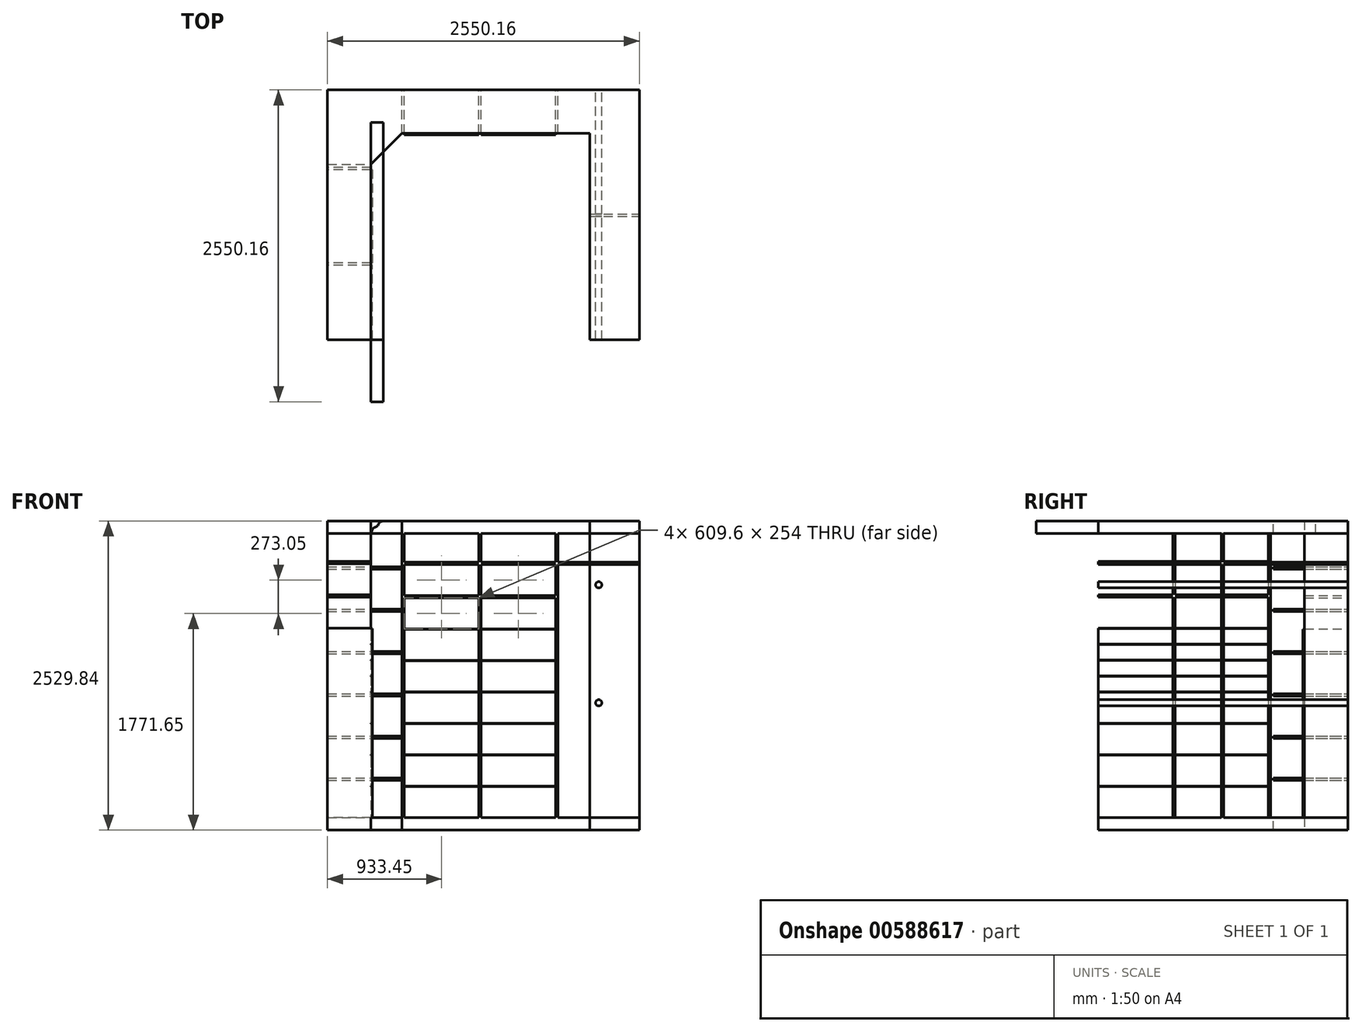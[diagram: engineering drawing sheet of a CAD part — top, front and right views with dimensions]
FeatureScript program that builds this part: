
annotation { "Feature Type Name" : "Feature", "Feature Type Description" : "" }
export const myFeature = defineFeature(function(context is Context, id is Id, definition is map)
    precondition{}
    {
        {
            var Q0;
            Q0=qCreatedBy(makeId("Top.planeOp"),FACE);
            var sketch = newSketch(context, id + "F0", { "sketchPlane" : qUnion([Q0])});
            skLineSegment(sketch, "E0.bottom", {"start": v(-1275.08, 1021.08) * mm, "end": v(1275.08, 1021.08) * mm});
            skLineSegment(sketch, "E0.top", {"start": v(-1275.08, -1021.08) * mm, "end": v(1275.08, -1021.08) * mm});
            skLineSegment(sketch, "E0.left", {"start": v(-1275.08, 1021.08) * mm, "end": v(-1275.08, -1021.08) * mm});
            skLineSegment(sketch, "E0.right", {"start": v(1275.08, 1021.08) * mm, "end": v(1275.08, -1021.08) * mm});
            skPoint(sketch, "E1", {"position": v(-1275.08, 0) * mm});
            skPoint(sketch, "E2", {"position": v(0, 1021.08) * mm});
            skArc(sketch, "E3", {"start": v(-68.07, -1021.08) * mm, "mid": v(139.94, -518.9) * mm, "end": v(642.11, -310.9) * mm, "construction": true});
            skLineSegment(sketch, "E4", {"start": v(642.11, -310.9) * mm, "end": v(642.11, -1021.08) * mm, "construction": true});
            skLineSegment(sketch, "E5", {"start": v(-919.48, -1021.08) * mm, "end": v(-919.48, 411.48) * mm});
            skLineSegment(sketch, "E6", {"start": v(-919.48, 411.48) * mm, "end": v(-665.48, 665.48) * mm});
            skLineSegment(sketch, "E7", {"start": v(-665.48, 665.48) * mm, "end": v(868.68, 665.48) * mm});
            skLineSegment(sketch, "E8", {"start": v(868.68, 665.48) * mm, "end": v(868.68, -1021.08) * mm});
            skLineSegment(sketch, "E9", {"start": v(-665.48, 1021.08) * mm, "end": v(-665.48, 411.48) * mm});
            skLineSegment(sketch, "E10", {"start": v(-665.48, 411.48) * mm, "end": v(-1275.08, 411.48) * mm});
            skSolve(sketch);
        }
        {
            var Q0;
            Q0=qCreatedBy(makeId("Front.planeOp"),FACE);
            var Q1;
            Q1=sQuery(id+"F0.wireOp",VERTEX,"E0.bottom.start");
            cPlane(context, id + "F1", {"entities" : qUnion([Q0, Q1]), "cplaneType" : CPlaneType.PLANE_POINT, "offset" : 25.4 * mm, "width" : 152.4 * mm, "height" : 152.4 * mm});
        }
        {
            var Q0;
            Q0=qCreatedBy(id+"F1.planeOp",FACE);
            var sketch = newSketch(context, id + "F2", { "sketchPlane" : qUnion([Q0])});
            skLineSegment(sketch, "E11.bottom", {"start": v(-1275.08, 2529.84) * mm, "end": v(1275.08, 2529.84) * mm});
            skLineSegment(sketch, "E11.top", {"start": v(-1275.08, 0) * mm, "end": v(1275.08, 0) * mm});
            skLineSegment(sketch, "E11.left", {"start": v(-1275.08, 2529.84) * mm, "end": v(-1275.08, 0) * mm});
            skLineSegment(sketch, "E11.right", {"start": v(1275.08, 2529.84) * mm, "end": v(1275.08, 0) * mm});
            skLineSegment(sketch, "E12", {"start": v(-1275.08, 101.6) * mm, "end": v(1275.08, 101.6) * mm});
            skLineSegment(sketch, "E13", {"start": v(-36.83, 101.6) * mm, "end": v(-36.83, 2529.84) * mm});
            skLineSegment(sketch, "E14", {"start": v(-17.78, 101.6) * mm, "end": v(-17.78, 2529.84) * mm});
            skLineSegment(sketch, "E15", {"start": v(-665.48, 2529.84) * mm, "end": v(-665.48, 0) * mm});
            skLineSegment(sketch, "E16", {"start": v(-646.43, 2529.84) * mm, "end": v(-646.43, 0) * mm});
            skLineSegment(sketch, "E17", {"start": v(591.82, 2529.84) * mm, "end": v(591.82, 101.6) * mm});
            skLineSegment(sketch, "E18", {"start": v(610.87, 2529.84) * mm, "end": v(610.87, 101.6) * mm});
            skLineSegment(sketch, "E19", {"start": v(-36.83, 245.4) * mm, "end": v(-17.78, 245.4) * mm, "construction": true});
            skLineSegment(sketch, "E20", {"start": v(-665.48, 245.4) * mm, "end": v(-646.43, 245.4) * mm, "construction": true});
            skLineSegment(sketch, "E21", {"start": v(591.82, 245.4) * mm, "end": v(610.87, 245.4) * mm, "construction": true});
            skLineSegment(sketch, "E22", {"start": v(-646.43, 245.4) * mm, "end": v(-36.83, 245.4) * mm, "construction": true});
            skLineSegment(sketch, "E23", {"start": v(-17.78, 245.4) * mm, "end": v(591.82, 245.4) * mm, "construction": true});
            skLineSegment(sketch, "E24", {"start": v(-646.43, 355.6) * mm, "end": v(591.82, 355.6) * mm});
            skLineSegment(sketch, "E25", {"start": v(-646.43, 358.78) * mm, "end": v(591.82, 358.78) * mm});
            skLineSegment(sketch, "E26.0.1.0", {"start": v(-646.43, 612.77) * mm, "end": v(591.82, 612.77) * mm});
            skLineSegment(sketch, "E26.0.1.1", {"start": v(-646.43, 615.95) * mm, "end": v(591.82, 615.95) * mm});
            skLineSegment(sketch, "E26.0.2.0", {"start": v(-646.43, 869.95) * mm, "end": v(591.82, 869.95) * mm});
            skLineSegment(sketch, "E26.0.2.1", {"start": v(-646.43, 873.12) * mm, "end": v(591.82, 873.12) * mm});
            skLineSegment(sketch, "E26.0.3.0", {"start": v(-646.43, 1127.12) * mm, "end": v(591.82, 1127.12) * mm});
            skLineSegment(sketch, "E26.0.3.1", {"start": v(-646.43, 1130.3) * mm, "end": v(591.82, 1130.3) * mm});
            skLineSegment(sketch, "E26.0.4.0", {"start": v(-646.43, 1384.3) * mm, "end": v(591.82, 1384.3) * mm});
            skLineSegment(sketch, "E26.0.4.1", {"start": v(-646.43, 1387.47) * mm, "end": v(591.82, 1387.47) * mm});
            skLineSegment(sketch, "E26.direction1", {"start": v(-646.43, 355.6) * mm, "end": v(-621.03, 355.6) * mm, "construction": true});
            skLineSegment(sketch, "E26.direction2", {"start": v(-646.43, 355.6) * mm, "end": v(-646.43, 612.77) * mm, "construction": true});
            skLineSegment(sketch, "E27.0.0.5", {"start": v(-646.43, 1641.47) * mm, "end": v(591.82, 1641.47) * mm});
            skLineSegment(sketch, "E27.3.0.5", {"start": v(-646.43, 1644.65) * mm, "end": v(591.82, 1644.65) * mm});
            skLineSegment(sketch, "E28", {"start": v(-1275.08, 2428.24) * mm, "end": v(1275.08, 2428.24) * mm});
            skLineSegment(sketch, "E29", {"start": v(-646.43, 1898.65) * mm, "end": v(591.82, 1898.65) * mm});
            skLineSegment(sketch, "E30", {"start": v(-646.43, 1917.7) * mm, "end": v(591.82, 1917.7) * mm});
            skLineSegment(sketch, "E31.0.1.0", {"start": v(-646.43, 2171.7) * mm, "end": v(591.82, 2171.7) * mm});
            skLineSegment(sketch, "E31.0.1.1", {"start": v(-646.43, 2190.75) * mm, "end": v(591.82, 2190.75) * mm});
            skLineSegment(sketch, "E31.direction1", {"start": v(-646.43, 1898.65) * mm, "end": v(-646.43, 1898.65) * mm});
            skLineSegment(sketch, "E31.direction2", {"start": v(-646.43, 1898.65) * mm, "end": v(-646.43, 2171.7) * mm, "construction": true});
            skCircle(sketch, "E32", {"center": v(942.98, 2006.6) * mm, "radius": 25.4 * mm});
            skLineSegment(sketch, "E33", {"start": v(610.87, 245.4) * mm, "end": v(1275.08, 245.4) * mm, "construction": true});
            skPoint(sketch, "E34", {"position": v(942.97, 245.4) * mm});
            skLineSegment(sketch, "E35", {"start": v(942.98, 2428.24) * mm, "end": v(942.98, 101.6) * mm, "construction": true});
            skLineSegment(sketch, "E36", {"start": v(610.87, 2171.7) * mm, "end": v(1275.08, 2171.7) * mm});
            skLineSegment(sketch, "E37", {"start": v(610.87, 2190.75) * mm, "end": v(1275.08, 2190.75) * mm});
            skCircle(sketch, "E38", {"center": v(942.98, 1041.4) * mm, "radius": 25.4 * mm});
            skLineSegment(sketch, "E39", {"start": v(-1275.08, 406.4) * mm, "end": v(-665.48, 406.4) * mm});
            skLineSegment(sketch, "E40", {"start": v(-1275.08, 425.45) * mm, "end": v(-665.48, 425.45) * mm});
            skLineSegment(sketch, "E41.0.1.0", {"start": v(-1275.08, 751.84) * mm, "end": v(-665.48, 751.84) * mm});
            skLineSegment(sketch, "E41.0.1.1", {"start": v(-1275.08, 770.9) * mm, "end": v(-665.48, 770.9) * mm});
            skLineSegment(sketch, "E41.0.2.0", {"start": v(-1275.08, 1097.28) * mm, "end": v(-665.48, 1097.28) * mm});
            skLineSegment(sketch, "E41.0.2.1", {"start": v(-1275.08, 1116.33) * mm, "end": v(-665.48, 1116.33) * mm});
            skLineSegment(sketch, "E41.0.3.0", {"start": v(-1275.08, 1442.72) * mm, "end": v(-665.48, 1442.72) * mm});
            skLineSegment(sketch, "E41.0.3.1", {"start": v(-1275.08, 1461.77) * mm, "end": v(-665.48, 1461.77) * mm});
            skLineSegment(sketch, "E41.0.4.0", {"start": v(-1275.08, 1788.16) * mm, "end": v(-665.48, 1788.16) * mm});
            skLineSegment(sketch, "E41.0.4.1", {"start": v(-1275.08, 1807.2) * mm, "end": v(-665.48, 1807.2) * mm});
            skLineSegment(sketch, "E41.0.5.0", {"start": v(-1275.08, 2133.6) * mm, "end": v(-665.48, 2133.6) * mm});
            skLineSegment(sketch, "E41.0.5.1", {"start": v(-1275.08, 2152.65) * mm, "end": v(-665.48, 2152.65) * mm});
            skLineSegment(sketch, "E41.direction1", {"start": v(-1275.08, 406.4) * mm, "end": v(-1275.08, 406.4) * mm});
            skLineSegment(sketch, "E41.direction2", {"start": v(-1275.08, 406.4) * mm, "end": v(-1275.08, 751.84) * mm, "construction": true});
            skLineSegment(sketch, "E42", {"start": v(-665.48, 245.4) * mm, "end": v(-1275.08, 245.4) * mm, "construction": true});
            skSolve(sketch);
        }
        {
            var Q0;
            Q0=qCreatedBy(makeId("Right.planeOp"),FACE);
            var Q1;
            Q1=sQuery(id+"F0.wireOp",VERTEX,"E0.left.end");
            cPlane(context, id + "F3", {"entities" : qUnion([Q0, Q1]), "cplaneType" : CPlaneType.PLANE_POINT, "offset" : 25.4 * mm, "width" : 152.4 * mm, "height" : 152.4 * mm});
        }
        {
            var Q0;
            Q0=qCreatedBy(id+"F3.planeOp",FACE);
            var sketch = newSketch(context, id + "F4", { "sketchPlane" : qUnion([Q0])});
            skLineSegment(sketch, "E43.bottom", {"start": v(-1021.08, 0) * mm, "end": v(1021.08, 0) * mm});
            skLineSegment(sketch, "E43.top", {"start": v(-1021.08, 2529.84) * mm, "end": v(1021.08, 2529.84) * mm});
            skLineSegment(sketch, "E43.left", {"start": v(-1021.08, 0) * mm, "end": v(-1021.08, 2529.84) * mm});
            skLineSegment(sketch, "E43.right", {"start": v(1021.08, 0) * mm, "end": v(1021.08, 2529.84) * mm});
            skLineSegment(sketch, "E44", {"start": v(1021.08, 2428.24) * mm, "end": v(-1021.08, 2428.24) * mm});
            skLineSegment(sketch, "E45", {"start": v(1021.08, 101.6) * mm, "end": v(-1021.08, 101.6) * mm});
            skLineSegment(sketch, "E46", {"start": v(-411.48, 2428.24) * mm, "end": v(-411.48, 101.6) * mm});
            skLineSegment(sketch, "E47", {"start": v(-392.43, 2428.24) * mm, "end": v(-392.43, 101.6) * mm});
            skLineSegment(sketch, "E48", {"start": v(369.57, 2428.24) * mm, "end": v(369.57, 101.6) * mm});
            skLineSegment(sketch, "E49", {"start": v(388.62, 2428.24) * mm, "end": v(388.62, 101.6) * mm});
            skLineSegment(sketch, "E50", {"start": v(-1021.08, 216.84) * mm, "end": v(-411.48, 216.84) * mm, "construction": true});
            skLineSegment(sketch, "E51", {"start": v(-411.48, 216.84) * mm, "end": v(-392.43, 216.84) * mm, "construction": true});
            skLineSegment(sketch, "E52", {"start": v(-392.43, 216.84) * mm, "end": v(369.57, 216.84) * mm, "construction": true});
            skLineSegment(sketch, "E53", {"start": v(369.57, 216.84) * mm, "end": v(388.62, 216.84) * mm, "construction": true});
            skLineSegment(sketch, "E54", {"start": v(388.62, 216.84) * mm, "end": v(1021.08, 216.84) * mm, "construction": true});
            skLineSegment(sketch, "E55", {"start": v(-1021.08, 1130.3) * mm, "end": v(369.57, 1130.3) * mm});
            skLineSegment(sketch, "E56", {"start": v(-1021.08, 1127.12) * mm, "end": v(369.57, 1127.12) * mm});
            skLineSegment(sketch, "E57", {"start": v(-1021.08, 355.6) * mm, "end": v(369.57, 355.6) * mm});
            skLineSegment(sketch, "E58", {"start": v(-1021.08, 358.77) * mm, "end": v(369.57, 358.77) * mm});
            skLineSegment(sketch, "E59.0.1.0", {"start": v(-1021.08, 1257.3) * mm, "end": v(369.57, 1257.3) * mm});
            skLineSegment(sketch, "E59.0.1.1", {"start": v(-1021.08, 1260.47) * mm, "end": v(369.57, 1260.47) * mm});
            skLineSegment(sketch, "E59.0.2.0", {"start": v(-1021.08, 1387.47) * mm, "end": v(369.57, 1387.47) * mm});
            skLineSegment(sketch, "E59.0.2.1", {"start": v(-1021.08, 1390.65) * mm, "end": v(369.57, 1390.65) * mm});
            skLineSegment(sketch, "E59.0.3.0", {"start": v(-1021.08, 1517.65) * mm, "end": v(369.57, 1517.65) * mm});
            skLineSegment(sketch, "E59.0.3.1", {"start": v(-1021.08, 1520.82) * mm, "end": v(369.57, 1520.82) * mm});
            skLineSegment(sketch, "E59.0.4.0", {"start": v(-1021.08, 1647.82) * mm, "end": v(369.57, 1647.82) * mm});
            skLineSegment(sketch, "E59.0.4.1", {"start": v(-1021.08, 1651) * mm, "end": v(369.57, 1651) * mm});
            skLineSegment(sketch, "E59.direction1", {"start": v(-1021.08, 1127.12) * mm, "end": v(-995.68, 1127.12) * mm, "construction": true});
            skLineSegment(sketch, "E59.direction2", {"start": v(-1021.08, 1127.12) * mm, "end": v(-1021.08, 1257.3) * mm, "construction": true});
            skLineSegment(sketch, "E60.0.1.0", {"start": v(-1021.08, 612.77) * mm, "end": v(369.57, 612.77) * mm});
            skLineSegment(sketch, "E60.0.1.1", {"start": v(-1021.08, 615.95) * mm, "end": v(369.57, 615.95) * mm});
            skLineSegment(sketch, "E60.0.2.0", {"start": v(-1021.08, 869.95) * mm, "end": v(369.57, 869.95) * mm});
            skLineSegment(sketch, "E60.0.2.1", {"start": v(-1021.08, 873.12) * mm, "end": v(369.57, 873.12) * mm});
            skLineSegment(sketch, "E60.direction1", {"start": v(-1021.08, 355.6) * mm, "end": v(-995.68, 355.6) * mm, "construction": true});
            skLineSegment(sketch, "E60.direction2", {"start": v(-1021.08, 355.6) * mm, "end": v(-1021.08, 612.77) * mm, "construction": true});
            skLineSegment(sketch, "E61", {"start": v(-1021.08, 1905) * mm, "end": v(369.57, 1905) * mm});
            skLineSegment(sketch, "E62", {"start": v(-1021.08, 1924.05) * mm, "end": v(369.57, 1924.05) * mm});
            skLineSegment(sketch, "E63", {"start": v(-1021.08, 2178.05) * mm, "end": v(369.57, 2178.05) * mm});
            skLineSegment(sketch, "E64", {"start": v(-1021.08, 2197.1) * mm, "end": v(369.57, 2197.1) * mm});
            skLineSegment(sketch, "E65", {"start": v(-504.08, 2428.24) * mm, "end": v(-504.08, 2197.1) * mm, "construction": true});
            skLineSegment(sketch, "E66", {"start": v(-504.08, 2197.1) * mm, "end": v(-504.08, 2178.05) * mm, "construction": true});
            skLineSegment(sketch, "E67", {"start": v(-504.08, 2178.05) * mm, "end": v(-504.08, 1924.05) * mm, "construction": true});
            skLineSegment(sketch, "E68", {"start": v(-504.08, 1924.05) * mm, "end": v(-504.08, 1905) * mm, "construction": true});
            skLineSegment(sketch, "E69", {"start": v(-504.08, 1905) * mm, "end": v(-504.08, 1651) * mm, "construction": true});
            skSolve(sketch);
        }
        {
            var Q0;
            Q0=qCreatedBy(makeId("Right.planeOp"),FACE);
            var Q1;
            Q1=sQuery(id+"F0.wireOp",VERTEX,"E0.right.end");
            cPlane(context, id + "F5", {"entities" : qUnion([Q0, Q1]), "cplaneType" : CPlaneType.PLANE_POINT, "offset" : 25.4 * mm, "width" : 152.4 * mm, "height" : 152.4 * mm});
        }
        {
            var Q0;
            Q0=qCreatedBy(id+"F5.planeOp",FACE);
            var sketch = newSketch(context, id + "F6", { "sketchPlane" : qUnion([Q0])});
            skLineSegment(sketch, "E70.bottom", {"start": v(-1021.08, 2529.84) * mm, "end": v(1021.08, 2529.84) * mm});
            skLineSegment(sketch, "E70.top", {"start": v(-1021.08, 0) * mm, "end": v(1021.08, 0) * mm});
            skLineSegment(sketch, "E70.left", {"start": v(-1021.08, 2529.84) * mm, "end": v(-1021.08, 0) * mm});
            skLineSegment(sketch, "E70.right", {"start": v(1021.08, 2529.84) * mm, "end": v(1021.08, 0) * mm});
            skLineSegment(sketch, "E71", {"start": v(5.08, 2529.84) * mm, "end": v(5.08, 101.6) * mm});
            skLineSegment(sketch, "E72", {"start": v(-13.97, 2529.84) * mm, "end": v(-13.97, 101.6) * mm});
            skLineSegment(sketch, "E73", {"start": v(1021.08, 101.6) * mm, "end": v(-1021.08, 101.6) * mm});
            skLineSegment(sketch, "E74", {"start": v(1021.08, 2428.24) * mm, "end": v(-1021.08, 2428.24) * mm});
            skLineSegment(sketch, "E75", {"start": v(1021.08, 2190.75) * mm, "end": v(-1021.08, 2190.75) * mm});
            skLineSegment(sketch, "E76", {"start": v(1021.08, 2171.7) * mm, "end": v(-1021.08, 2171.7) * mm});
            skSolve(sketch);
        }
        {
            var Q0;
            {var subQ0=sQuery(id+"F2.wireOp",EDGE,"E26.0.4.1");var subQ1=sQuery(id+"F2.wireOp",EDGE,"E13");var subQ2=makeQuery(id+"F2.imprint","INTERSECT",VERTEX,{"derivedFrom":[subQ1,subQ0]});Q0=makeQuery(id+"F2.imprint","IMPRINT",FACE,{"disambiguationData":[TD([[makeQuery(id+"F2.imprint","IMPRINT",EDGE,{"disambiguationData":[TD([[subQ2,-1.0]])],"derivedFrom":subQ1}),-1.0]])]});}
            var Q1;
            {var subQ0=sQuery(id+"F2.wireOp",EDGE,"E26.0.4.0");var subQ1=sQuery(id+"F2.wireOp",EDGE,"E13");var subQ2=makeQuery(id+"F2.imprint","INTERSECT",VERTEX,{"derivedFrom":[subQ1,subQ0]});Q1=makeQuery(id+"F2.imprint","IMPRINT",FACE,{"disambiguationData":[TD([[makeQuery(id+"F2.imprint","IMPRINT",EDGE,{"disambiguationData":[TD([[subQ2,-1.0]])],"derivedFrom":subQ1}),-1.0]])]});}
            var Q2;
            {var subQ0=sQuery(id+"F2.wireOp",EDGE,"E26.0.3.1");var subQ1=sQuery(id+"F2.wireOp",EDGE,"E13");var subQ2=makeQuery(id+"F2.imprint","INTERSECT",VERTEX,{"derivedFrom":[subQ1,subQ0]});Q2=makeQuery(id+"F2.imprint","IMPRINT",FACE,{"disambiguationData":[TD([[makeQuery(id+"F2.imprint","IMPRINT",EDGE,{"disambiguationData":[TD([[subQ2,-1.0]])],"derivedFrom":subQ1}),-1.0]])]});}
            var Q3;
            {var subQ0=sQuery(id+"F2.wireOp",EDGE,"E26.0.3.0");var subQ1=sQuery(id+"F2.wireOp",EDGE,"E13");var subQ2=makeQuery(id+"F2.imprint","INTERSECT",VERTEX,{"derivedFrom":[subQ1,subQ0]});Q3=makeQuery(id+"F2.imprint","IMPRINT",FACE,{"disambiguationData":[TD([[makeQuery(id+"F2.imprint","IMPRINT",EDGE,{"disambiguationData":[TD([[subQ2,-1.0]])],"derivedFrom":subQ1}),-1.0]])]});}
            var Q4;
            {var subQ0=sQuery(id+"F2.wireOp",EDGE,"E26.0.2.1");var subQ1=sQuery(id+"F2.wireOp",EDGE,"E13");var subQ2=makeQuery(id+"F2.imprint","INTERSECT",VERTEX,{"derivedFrom":[subQ1,subQ0]});Q4=makeQuery(id+"F2.imprint","IMPRINT",FACE,{"disambiguationData":[TD([[makeQuery(id+"F2.imprint","IMPRINT",EDGE,{"disambiguationData":[TD([[subQ2,-1.0]])],"derivedFrom":subQ1}),-1.0]])]});}
            var Q5;
            {var subQ0=sQuery(id+"F2.wireOp",EDGE,"E26.0.2.0");var subQ1=sQuery(id+"F2.wireOp",EDGE,"E13");var subQ2=makeQuery(id+"F2.imprint","INTERSECT",VERTEX,{"derivedFrom":[subQ1,subQ0]});Q5=makeQuery(id+"F2.imprint","IMPRINT",FACE,{"disambiguationData":[TD([[makeQuery(id+"F2.imprint","IMPRINT",EDGE,{"disambiguationData":[TD([[subQ2,-1.0]])],"derivedFrom":subQ1}),-1.0]])]});}
            var Q6;
            {var subQ0=sQuery(id+"F2.wireOp",EDGE,"E26.0.1.1");var subQ1=sQuery(id+"F2.wireOp",EDGE,"E13");var subQ2=makeQuery(id+"F2.imprint","INTERSECT",VERTEX,{"derivedFrom":[subQ1,subQ0]});Q6=makeQuery(id+"F2.imprint","IMPRINT",FACE,{"disambiguationData":[TD([[makeQuery(id+"F2.imprint","IMPRINT",EDGE,{"disambiguationData":[TD([[subQ2,-1.0]])],"derivedFrom":subQ1}),-1.0]])]});}
            var Q7;
            {var subQ0=sQuery(id+"F2.wireOp",EDGE,"E26.0.1.0");var subQ1=sQuery(id+"F2.wireOp",EDGE,"E13");var subQ2=makeQuery(id+"F2.imprint","INTERSECT",VERTEX,{"derivedFrom":[subQ1,subQ0]});Q7=makeQuery(id+"F2.imprint","IMPRINT",FACE,{"disambiguationData":[TD([[makeQuery(id+"F2.imprint","IMPRINT",EDGE,{"disambiguationData":[TD([[subQ2,-1.0]])],"derivedFrom":subQ1}),-1.0]])]});}
            var Q8;
            {var subQ0=sQuery(id+"F2.wireOp",EDGE,"E25");var subQ1=sQuery(id+"F2.wireOp",EDGE,"E13");var subQ2=makeQuery(id+"F2.imprint","INTERSECT",VERTEX,{"derivedFrom":[subQ1,subQ0]});Q8=makeQuery(id+"F2.imprint","IMPRINT",FACE,{"disambiguationData":[TD([[makeQuery(id+"F2.imprint","IMPRINT",EDGE,{"disambiguationData":[TD([[subQ2,-1.0]])],"derivedFrom":subQ1}),-1.0]])]});}
            var Q9;
            {var subQ0=sQuery(id+"F2.wireOp",EDGE,"E24");var subQ1=sQuery(id+"F2.wireOp",EDGE,"E13");var subQ2=makeQuery(id+"F2.imprint","INTERSECT",VERTEX,{"derivedFrom":[subQ1,subQ0]});Q9=makeQuery(id+"F2.imprint","IMPRINT",FACE,{"disambiguationData":[TD([[makeQuery(id+"F2.imprint","IMPRINT",EDGE,{"disambiguationData":[TD([[subQ2,-1.0]])],"derivedFrom":subQ1}),-1.0]])]});}
            var Q10;
            {var subQ0=sQuery(id+"F2.wireOp",EDGE,"E13");var subQ1=sQuery(id+"F2.wireOp",EDGE,"E12");var subQ2=makeQuery(id+"F2.imprint","INTERSECT",VERTEX,{"derivedFrom":[subQ1,subQ0]});Q10=makeQuery(id+"F2.imprint","IMPRINT",FACE,{"disambiguationData":[TD([[makeQuery(id+"F2.imprint","IMPRINT",EDGE,{"disambiguationData":[TD([[subQ2,-1.0]])],"derivedFrom":subQ1}),1.0]])]});}
            extrude(context, id + "F7", {"entities" : qUnion([Q0, Q1, Q2, Q3, Q4, Q5, Q6, Q7, Q8, Q9, Q10]), "depth" : 25.4 * mm, "offsetDistance" : 25.4 * mm});
        }
        {
            var Q0;
            {var subQ11=sQuery(id+"F2.wireOp",EDGE,"E15");var subQ12=sQuery(id+"F2.wireOp",EDGE,"E12");var subQ13=makeQuery(id+"F2.imprint","INTERSECT",VERTEX,{"derivedFrom":[subQ12,subQ11]});Q0=makeQuery(id+"F2.imprint","IMPRINT",FACE,{"disambiguationData":[TD([[makeQuery(id+"F2.imprint","IMPRINT",EDGE,{"disambiguationData":[TD([[subQ13,-1.0]])],"derivedFrom":subQ12}),1.0]])]});}
            var Q1;
            {var subQ0=sQuery(id+"F2.wireOp",EDGE,"E24");var subQ1=sQuery(id+"F2.wireOp",EDGE,"E13");var subQ2=makeQuery(id+"F2.imprint","INTERSECT",VERTEX,{"derivedFrom":[subQ1,subQ0]});Q1=makeQuery(id+"F2.imprint","IMPRINT",FACE,{"disambiguationData":[TD([[makeQuery(id+"F2.imprint","IMPRINT",EDGE,{"disambiguationData":[TD([[subQ2,-1.0]])],"derivedFrom":subQ1}),1.0]])]});}
            var Q2;
            {var subQ0=sQuery(id+"F2.wireOp",EDGE,"E24");var subQ1=sQuery(id+"F2.wireOp",EDGE,"E13");var subQ2=makeQuery(id+"F2.imprint","INTERSECT",VERTEX,{"derivedFrom":[subQ1,subQ0]});Q2=makeQuery(id+"F2.imprint","IMPRINT",FACE,{"disambiguationData":[TD([[makeQuery(id+"F2.imprint","IMPRINT",EDGE,{"disambiguationData":[TD([[subQ2,-1.0]])],"derivedFrom":subQ1}),-1.0]])]});}
            var Q3;
            {var subQ0=sQuery(id+"F2.wireOp",EDGE,"E24");var subQ1=sQuery(id+"F2.wireOp",EDGE,"E14");var subQ2=makeQuery(id+"F2.imprint","INTERSECT",VERTEX,{"derivedFrom":[subQ1,subQ0]});Q3=makeQuery(id+"F2.imprint","IMPRINT",FACE,{"disambiguationData":[TD([[makeQuery(id+"F2.imprint","IMPRINT",EDGE,{"disambiguationData":[TD([[subQ2,-1.0]])],"derivedFrom":subQ1}),-1.0]])]});}
            var Q4;
            {var subQ0=sQuery(id+"F2.wireOp",EDGE,"E26.0.1.0");var subQ1=sQuery(id+"F2.wireOp",EDGE,"E13");var subQ2=makeQuery(id+"F2.imprint","INTERSECT",VERTEX,{"derivedFrom":[subQ1,subQ0]});Q4=makeQuery(id+"F2.imprint","IMPRINT",FACE,{"disambiguationData":[TD([[makeQuery(id+"F2.imprint","IMPRINT",EDGE,{"disambiguationData":[TD([[subQ2,-1.0]])],"derivedFrom":subQ1}),1.0]])]});}
            var Q5;
            {var subQ0=sQuery(id+"F2.wireOp",EDGE,"E26.0.1.0");var subQ1=sQuery(id+"F2.wireOp",EDGE,"E13");var subQ2=makeQuery(id+"F2.imprint","INTERSECT",VERTEX,{"derivedFrom":[subQ1,subQ0]});Q5=makeQuery(id+"F2.imprint","IMPRINT",FACE,{"disambiguationData":[TD([[makeQuery(id+"F2.imprint","IMPRINT",EDGE,{"disambiguationData":[TD([[subQ2,-1.0]])],"derivedFrom":subQ1}),-1.0]])]});}
            var Q6;
            {var subQ0=sQuery(id+"F2.wireOp",EDGE,"E26.0.1.0");var subQ1=sQuery(id+"F2.wireOp",EDGE,"E14");var subQ2=makeQuery(id+"F2.imprint","INTERSECT",VERTEX,{"derivedFrom":[subQ1,subQ0]});Q6=makeQuery(id+"F2.imprint","IMPRINT",FACE,{"disambiguationData":[TD([[makeQuery(id+"F2.imprint","IMPRINT",EDGE,{"disambiguationData":[TD([[subQ2,-1.0]])],"derivedFrom":subQ1}),-1.0]])]});}
            var Q7;
            {var subQ0=sQuery(id+"F2.wireOp",EDGE,"E25");var subQ1=sQuery(id+"F2.wireOp",EDGE,"E13");var subQ2=makeQuery(id+"F2.imprint","INTERSECT",VERTEX,{"derivedFrom":[subQ1,subQ0]});Q7=makeQuery(id+"F2.imprint","IMPRINT",FACE,{"disambiguationData":[TD([[makeQuery(id+"F2.imprint","IMPRINT",EDGE,{"disambiguationData":[TD([[subQ2,-1.0]])],"derivedFrom":subQ1}),-1.0]])]});}
            var Q8;
            {var subQ0=sQuery(id+"F2.wireOp",EDGE,"E13");var subQ1=sQuery(id+"F2.wireOp",EDGE,"E12");var subQ2=makeQuery(id+"F2.imprint","INTERSECT",VERTEX,{"derivedFrom":[subQ1,subQ0]});Q8=makeQuery(id+"F2.imprint","IMPRINT",FACE,{"disambiguationData":[TD([[makeQuery(id+"F2.imprint","IMPRINT",EDGE,{"disambiguationData":[TD([[subQ2,-1.0]])],"derivedFrom":subQ1}),1.0]])]});}
            var Q9;
            {var subQ0=sQuery(id+"F2.wireOp",EDGE,"E26.0.2.0");var subQ1=sQuery(id+"F2.wireOp",EDGE,"E13");var subQ2=makeQuery(id+"F2.imprint","INTERSECT",VERTEX,{"derivedFrom":[subQ1,subQ0]});Q9=makeQuery(id+"F2.imprint","IMPRINT",FACE,{"disambiguationData":[TD([[makeQuery(id+"F2.imprint","IMPRINT",EDGE,{"disambiguationData":[TD([[subQ2,-1.0]])],"derivedFrom":subQ1}),1.0]])]});}
            var Q10;
            {var subQ0=sQuery(id+"F2.wireOp",EDGE,"E26.0.2.0");var subQ1=sQuery(id+"F2.wireOp",EDGE,"E13");var subQ2=makeQuery(id+"F2.imprint","INTERSECT",VERTEX,{"derivedFrom":[subQ1,subQ0]});Q10=makeQuery(id+"F2.imprint","IMPRINT",FACE,{"disambiguationData":[TD([[makeQuery(id+"F2.imprint","IMPRINT",EDGE,{"disambiguationData":[TD([[subQ2,-1.0]])],"derivedFrom":subQ1}),-1.0]])]});}
            var Q11;
            {var subQ0=sQuery(id+"F2.wireOp",EDGE,"E26.0.2.0");var subQ1=sQuery(id+"F2.wireOp",EDGE,"E14");var subQ2=makeQuery(id+"F2.imprint","INTERSECT",VERTEX,{"derivedFrom":[subQ1,subQ0]});Q11=makeQuery(id+"F2.imprint","IMPRINT",FACE,{"disambiguationData":[TD([[makeQuery(id+"F2.imprint","IMPRINT",EDGE,{"disambiguationData":[TD([[subQ2,-1.0]])],"derivedFrom":subQ1}),-1.0]])]});}
            var Q12;
            {var subQ0=sQuery(id+"F2.wireOp",EDGE,"E26.0.1.1");var subQ1=sQuery(id+"F2.wireOp",EDGE,"E13");var subQ2=makeQuery(id+"F2.imprint","INTERSECT",VERTEX,{"derivedFrom":[subQ1,subQ0]});Q12=makeQuery(id+"F2.imprint","IMPRINT",FACE,{"disambiguationData":[TD([[makeQuery(id+"F2.imprint","IMPRINT",EDGE,{"disambiguationData":[TD([[subQ2,-1.0]])],"derivedFrom":subQ1}),-1.0]])]});}
            var Q13;
            {var subQ0=sQuery(id+"F2.wireOp",EDGE,"E26.0.2.1");var subQ1=sQuery(id+"F2.wireOp",EDGE,"E13");var subQ2=makeQuery(id+"F2.imprint","INTERSECT",VERTEX,{"derivedFrom":[subQ1,subQ0]});Q13=makeQuery(id+"F2.imprint","IMPRINT",FACE,{"disambiguationData":[TD([[makeQuery(id+"F2.imprint","IMPRINT",EDGE,{"disambiguationData":[TD([[subQ2,-1.0]])],"derivedFrom":subQ1}),-1.0]])]});}
            var Q14;
            {var subQ0=sQuery(id+"F2.wireOp",EDGE,"E26.0.3.0");var subQ1=sQuery(id+"F2.wireOp",EDGE,"E13");var subQ2=makeQuery(id+"F2.imprint","INTERSECT",VERTEX,{"derivedFrom":[subQ1,subQ0]});Q14=makeQuery(id+"F2.imprint","IMPRINT",FACE,{"disambiguationData":[TD([[makeQuery(id+"F2.imprint","IMPRINT",EDGE,{"disambiguationData":[TD([[subQ2,-1.0]])],"derivedFrom":subQ1}),1.0]])]});}
            var Q15;
            {var subQ0=sQuery(id+"F2.wireOp",EDGE,"E26.0.3.0");var subQ1=sQuery(id+"F2.wireOp",EDGE,"E13");var subQ2=makeQuery(id+"F2.imprint","INTERSECT",VERTEX,{"derivedFrom":[subQ1,subQ0]});Q15=makeQuery(id+"F2.imprint","IMPRINT",FACE,{"disambiguationData":[TD([[makeQuery(id+"F2.imprint","IMPRINT",EDGE,{"disambiguationData":[TD([[subQ2,-1.0]])],"derivedFrom":subQ1}),-1.0]])]});}
            var Q16;
            {var subQ0=sQuery(id+"F2.wireOp",EDGE,"E26.0.3.0");var subQ1=sQuery(id+"F2.wireOp",EDGE,"E14");var subQ2=makeQuery(id+"F2.imprint","INTERSECT",VERTEX,{"derivedFrom":[subQ1,subQ0]});Q16=makeQuery(id+"F2.imprint","IMPRINT",FACE,{"disambiguationData":[TD([[makeQuery(id+"F2.imprint","IMPRINT",EDGE,{"disambiguationData":[TD([[subQ2,-1.0]])],"derivedFrom":subQ1}),-1.0]])]});}
            var Q17;
            {var subQ0=sQuery(id+"F2.wireOp",EDGE,"E26.0.3.1");var subQ1=sQuery(id+"F2.wireOp",EDGE,"E13");var subQ2=makeQuery(id+"F2.imprint","INTERSECT",VERTEX,{"derivedFrom":[subQ1,subQ0]});Q17=makeQuery(id+"F2.imprint","IMPRINT",FACE,{"disambiguationData":[TD([[makeQuery(id+"F2.imprint","IMPRINT",EDGE,{"disambiguationData":[TD([[subQ2,-1.0]])],"derivedFrom":subQ1}),-1.0]])]});}
            var Q18;
            {var subQ0=sQuery(id+"F2.wireOp",EDGE,"E26.0.4.0");var subQ1=sQuery(id+"F2.wireOp",EDGE,"E13");var subQ2=makeQuery(id+"F2.imprint","INTERSECT",VERTEX,{"derivedFrom":[subQ1,subQ0]});Q18=makeQuery(id+"F2.imprint","IMPRINT",FACE,{"disambiguationData":[TD([[makeQuery(id+"F2.imprint","IMPRINT",EDGE,{"disambiguationData":[TD([[subQ2,-1.0]])],"derivedFrom":subQ1}),1.0]])]});}
            var Q19;
            {var subQ0=sQuery(id+"F2.wireOp",EDGE,"E26.0.4.0");var subQ1=sQuery(id+"F2.wireOp",EDGE,"E13");var subQ2=makeQuery(id+"F2.imprint","INTERSECT",VERTEX,{"derivedFrom":[subQ1,subQ0]});Q19=makeQuery(id+"F2.imprint","IMPRINT",FACE,{"disambiguationData":[TD([[makeQuery(id+"F2.imprint","IMPRINT",EDGE,{"disambiguationData":[TD([[subQ2,-1.0]])],"derivedFrom":subQ1}),-1.0]])]});}
            var Q20;
            {var subQ0=sQuery(id+"F2.wireOp",EDGE,"E26.0.4.0");var subQ1=sQuery(id+"F2.wireOp",EDGE,"E14");var subQ2=makeQuery(id+"F2.imprint","INTERSECT",VERTEX,{"derivedFrom":[subQ1,subQ0]});Q20=makeQuery(id+"F2.imprint","IMPRINT",FACE,{"disambiguationData":[TD([[makeQuery(id+"F2.imprint","IMPRINT",EDGE,{"disambiguationData":[TD([[subQ2,-1.0]])],"derivedFrom":subQ1}),-1.0]])]});}
            var Q21;
            {var subQ0=sQuery(id+"F2.wireOp",EDGE,"E26.0.4.1");var subQ1=sQuery(id+"F2.wireOp",EDGE,"E13");var subQ2=makeQuery(id+"F2.imprint","INTERSECT",VERTEX,{"derivedFrom":[subQ1,subQ0]});Q21=makeQuery(id+"F2.imprint","IMPRINT",FACE,{"disambiguationData":[TD([[makeQuery(id+"F2.imprint","IMPRINT",EDGE,{"disambiguationData":[TD([[subQ2,-1.0]])],"derivedFrom":subQ1}),-1.0]])]});}
            var Q22;
            {var subQ0=sQuery(id+"F2.wireOp",EDGE,"E27.0.0.5");var subQ1=sQuery(id+"F2.wireOp",EDGE,"E13");var subQ2=makeQuery(id+"F2.imprint","INTERSECT",VERTEX,{"derivedFrom":[subQ1,subQ0]});Q22=makeQuery(id+"F2.imprint","IMPRINT",FACE,{"disambiguationData":[TD([[makeQuery(id+"F2.imprint","IMPRINT",EDGE,{"disambiguationData":[TD([[subQ2,-1.0]])],"derivedFrom":subQ1}),1.0]])]});}
            var Q23;
            {var subQ0=sQuery(id+"F2.wireOp",EDGE,"E27.0.0.5");var subQ1=sQuery(id+"F2.wireOp",EDGE,"E13");var subQ2=makeQuery(id+"F2.imprint","INTERSECT",VERTEX,{"derivedFrom":[subQ1,subQ0]});Q23=makeQuery(id+"F2.imprint","IMPRINT",FACE,{"disambiguationData":[TD([[makeQuery(id+"F2.imprint","IMPRINT",EDGE,{"disambiguationData":[TD([[subQ2,-1.0]])],"derivedFrom":subQ1}),-1.0]])]});}
            var Q24;
            {var subQ0=sQuery(id+"F2.wireOp",EDGE,"E27.0.0.5");var subQ1=sQuery(id+"F2.wireOp",EDGE,"E14");var subQ2=makeQuery(id+"F2.imprint","INTERSECT",VERTEX,{"derivedFrom":[subQ1,subQ0]});Q24=makeQuery(id+"F2.imprint","IMPRINT",FACE,{"disambiguationData":[TD([[makeQuery(id+"F2.imprint","IMPRINT",EDGE,{"disambiguationData":[TD([[subQ2,-1.0]])],"derivedFrom":subQ1}),-1.0]])]});}
            var Q25;
            {var subQ0=sQuery(id+"F2.wireOp",EDGE,"E27.3.0.5");var subQ1=sQuery(id+"F2.wireOp",EDGE,"E13");var subQ2=makeQuery(id+"F2.imprint","INTERSECT",VERTEX,{"derivedFrom":[subQ1,subQ0]});Q25=makeQuery(id+"F2.imprint","IMPRINT",FACE,{"disambiguationData":[TD([[makeQuery(id+"F2.imprint","IMPRINT",EDGE,{"disambiguationData":[TD([[subQ2,-1.0]])],"derivedFrom":subQ1}),-1.0]])]});}
            var Q26;
            {var subQ0=sQuery(id+"F2.wireOp",EDGE,"E29");var subQ1=sQuery(id+"F2.wireOp",EDGE,"E13");var subQ2=makeQuery(id+"F2.imprint","INTERSECT",VERTEX,{"derivedFrom":[subQ1,subQ0]});Q26=makeQuery(id+"F2.imprint","IMPRINT",FACE,{"disambiguationData":[TD([[makeQuery(id+"F2.imprint","IMPRINT",EDGE,{"disambiguationData":[TD([[subQ2,-1.0]])],"derivedFrom":subQ1}),1.0]])]});}
            var Q27;
            {var subQ0=sQuery(id+"F2.wireOp",EDGE,"E29");var subQ1=sQuery(id+"F2.wireOp",EDGE,"E13");var subQ2=makeQuery(id+"F2.imprint","INTERSECT",VERTEX,{"derivedFrom":[subQ1,subQ0]});Q27=makeQuery(id+"F2.imprint","IMPRINT",FACE,{"disambiguationData":[TD([[makeQuery(id+"F2.imprint","IMPRINT",EDGE,{"disambiguationData":[TD([[subQ2,-1.0]])],"derivedFrom":subQ1}),-1.0]])]});}
            var Q28;
            {var subQ0=sQuery(id+"F2.wireOp",EDGE,"E29");var subQ1=sQuery(id+"F2.wireOp",EDGE,"E14");var subQ2=makeQuery(id+"F2.imprint","INTERSECT",VERTEX,{"derivedFrom":[subQ1,subQ0]});Q28=makeQuery(id+"F2.imprint","IMPRINT",FACE,{"disambiguationData":[TD([[makeQuery(id+"F2.imprint","IMPRINT",EDGE,{"disambiguationData":[TD([[subQ2,-1.0]])],"derivedFrom":subQ1}),-1.0]])]});}
            var Q29;
            {var subQ0=sQuery(id+"F2.wireOp",EDGE,"E30");var subQ1=sQuery(id+"F2.wireOp",EDGE,"E13");var subQ2=makeQuery(id+"F2.imprint","INTERSECT",VERTEX,{"derivedFrom":[subQ1,subQ0]});Q29=makeQuery(id+"F2.imprint","IMPRINT",FACE,{"disambiguationData":[TD([[makeQuery(id+"F2.imprint","IMPRINT",EDGE,{"disambiguationData":[TD([[subQ2,-1.0]])],"derivedFrom":subQ1}),-1.0]])]});}
            var Q30;
            {var subQ0=sQuery(id+"F2.wireOp",EDGE,"E31.0.1.0");var subQ1=sQuery(id+"F2.wireOp",EDGE,"E13");var subQ2=makeQuery(id+"F2.imprint","INTERSECT",VERTEX,{"derivedFrom":[subQ1,subQ0]});Q30=makeQuery(id+"F2.imprint","IMPRINT",FACE,{"disambiguationData":[TD([[makeQuery(id+"F2.imprint","IMPRINT",EDGE,{"disambiguationData":[TD([[subQ2,-1.0]])],"derivedFrom":subQ1}),1.0]])]});}
            var Q31;
            {var subQ0=sQuery(id+"F2.wireOp",EDGE,"E31.0.1.0");var subQ1=sQuery(id+"F2.wireOp",EDGE,"E14");var subQ2=makeQuery(id+"F2.imprint","INTERSECT",VERTEX,{"derivedFrom":[subQ1,subQ0]});Q31=makeQuery(id+"F2.imprint","IMPRINT",FACE,{"disambiguationData":[TD([[makeQuery(id+"F2.imprint","IMPRINT",EDGE,{"disambiguationData":[TD([[subQ2,-1.0]])],"derivedFrom":subQ1}),-1.0]])]});}
            var Q32;
            {var subQ0=sQuery(id+"F2.wireOp",EDGE,"E31.0.1.1");var subQ1=sQuery(id+"F2.wireOp",EDGE,"E13");var subQ2=makeQuery(id+"F2.imprint","INTERSECT",VERTEX,{"derivedFrom":[subQ1,subQ0]});Q32=makeQuery(id+"F2.imprint","IMPRINT",FACE,{"disambiguationData":[TD([[makeQuery(id+"F2.imprint","IMPRINT",EDGE,{"disambiguationData":[TD([[subQ2,-1.0]])],"derivedFrom":subQ1}),-1.0]])]});}
            var Q33;
            {var subQ0=sQuery(id+"F2.wireOp",EDGE,"E15");var subQ1=sQuery(id+"F2.wireOp",EDGE,"E11.bottom");var subQ2=makeQuery(id+"F2.imprint","INTERSECT",VERTEX,{"derivedFrom":[subQ1,subQ0]});Q33=makeQuery(id+"F2.imprint","IMPRINT",FACE,{"disambiguationData":[TD([[makeQuery(id+"F2.imprint","IMPRINT",EDGE,{"disambiguationData":[TD([[subQ2,-1.0]])],"derivedFrom":subQ1}),-1.0]])]});}
            var Q34;
            {var subQ0=sQuery(id+"F2.wireOp",EDGE,"E13");var subQ1=sQuery(id+"F2.wireOp",EDGE,"E11.bottom");var subQ2=makeQuery(id+"F2.imprint","INTERSECT",VERTEX,{"derivedFrom":[subQ1,subQ0]});Q34=makeQuery(id+"F2.imprint","IMPRINT",FACE,{"disambiguationData":[TD([[makeQuery(id+"F2.imprint","IMPRINT",EDGE,{"disambiguationData":[TD([[subQ2,1.0]])],"derivedFrom":subQ1}),-1.0]])]});}
            var Q35;
            {var subQ0=sQuery(id+"F2.wireOp",EDGE,"E13");var subQ1=sQuery(id+"F2.wireOp",EDGE,"E11.bottom");var subQ2=makeQuery(id+"F2.imprint","INTERSECT",VERTEX,{"derivedFrom":[subQ1,subQ0]});Q35=makeQuery(id+"F2.imprint","IMPRINT",FACE,{"disambiguationData":[TD([[makeQuery(id+"F2.imprint","IMPRINT",EDGE,{"disambiguationData":[TD([[subQ2,-1.0]])],"derivedFrom":subQ1}),-1.0]])]});}
            var Q36;
            {var subQ0=sQuery(id+"F2.wireOp",EDGE,"E14");var subQ1=sQuery(id+"F2.wireOp",EDGE,"E11.bottom");var subQ2=makeQuery(id+"F2.imprint","INTERSECT",VERTEX,{"derivedFrom":[subQ1,subQ0]});Q36=makeQuery(id+"F2.imprint","IMPRINT",FACE,{"disambiguationData":[TD([[makeQuery(id+"F2.imprint","IMPRINT",EDGE,{"disambiguationData":[TD([[subQ2,-1.0]])],"derivedFrom":subQ1}),-1.0]])]});}
            var Q37;
            {var subQ0=sQuery(id+"F2.wireOp",EDGE,"E31.0.1.0");var subQ1=sQuery(id+"F2.wireOp",EDGE,"E13");var subQ2=makeQuery(id+"F2.imprint","INTERSECT",VERTEX,{"derivedFrom":[subQ1,subQ0]});Q37=makeQuery(id+"F2.imprint","IMPRINT",FACE,{"disambiguationData":[TD([[makeQuery(id+"F2.imprint","IMPRINT",EDGE,{"disambiguationData":[TD([[subQ2,-1.0]])],"derivedFrom":subQ1}),-1.0]])]});}
            var Q38;
            {var subQ0=sQuery(id+"F2.wireOp",EDGE,"E17");var subQ1=sQuery(id+"F2.wireOp",EDGE,"E11.bottom");var subQ2=makeQuery(id+"F2.imprint","INTERSECT",VERTEX,{"derivedFrom":[subQ1,subQ0]});Q38=makeQuery(id+"F2.imprint","IMPRINT",FACE,{"disambiguationData":[TD([[makeQuery(id+"F2.imprint","IMPRINT",EDGE,{"disambiguationData":[TD([[subQ2,-1.0]])],"derivedFrom":subQ1}),-1.0]])]});}
            var Q39;
            {var subQ0=sQuery(id+"F2.wireOp",EDGE,"E11.right");var subQ1=sQuery(id+"F2.wireOp",EDGE,"E11.bottom");var subQ2=makeQuery(id+"F2.imprint","INTERSECT",VERTEX,{"derivedFrom":[subQ1,subQ0]});Q39=makeQuery(id+"F2.imprint","IMPRINT",FACE,{"disambiguationData":[TD([[makeQuery(id+"F2.imprint","IMPRINT",EDGE,{"disambiguationData":[TD([[subQ2,1.0]])],"derivedFrom":subQ1}),-1.0]])]});}
            var Q40;
            {var subQ0=sQuery(id+"F2.wireOp",EDGE,"E17");var subQ8=sQuery(id+"F2.wireOp",EDGE,"E12");var subQ9=makeQuery(id+"F2.imprint","INTERSECT",VERTEX,{"derivedFrom":[subQ8,subQ0]});Q40=makeQuery(id+"F2.imprint","IMPRINT",FACE,{"disambiguationData":[TD([[makeQuery(id+"F2.imprint","IMPRINT",EDGE,{"disambiguationData":[TD([[subQ9,-1.0]])],"derivedFrom":subQ8}),1.0]])]});}
            var Q41;
            {var subQ0=sQuery(id+"F2.wireOp",EDGE,"E15");var subQ1=sQuery(id+"F2.wireOp",EDGE,"E11.top");var subQ2=makeQuery(id+"F2.imprint","INTERSECT",VERTEX,{"derivedFrom":[subQ1,subQ0]});Q41=makeQuery(id+"F2.imprint","IMPRINT",FACE,{"disambiguationData":[TD([[makeQuery(id+"F2.imprint","IMPRINT",EDGE,{"disambiguationData":[TD([[subQ2,-1.0]])],"derivedFrom":subQ1}),1.0]])]});}
            var Q42;
            {var subQ5=sQuery(id+"F2.wireOp",EDGE,"E11.right");var subQ6=sQuery(id+"F2.wireOp",EDGE,"E11.top");var subQ7=makeQuery(id+"F2.imprint","INTERSECT",VERTEX,{"derivedFrom":[subQ6,subQ5]});Q42=makeQuery(id+"F2.imprint","IMPRINT",FACE,{"disambiguationData":[TD([[makeQuery(id+"F2.imprint","IMPRINT",EDGE,{"disambiguationData":[TD([[subQ7,1.0]])],"derivedFrom":subQ6}),1.0]])]});}
            var Q43;
            {var subQ0=sQuery(id+"F2.wireOp",EDGE,"E36");Q43=makeQuery(id+"F2.imprint","IMPRINT",FACE,{"disambiguationData":[TD([[makeQuery(id+"F2.imprint","IMPRINT",EDGE,{"derivedFrom":subQ0}),1.0]])]});}
            var Q44;
            Q44=sQuery(id+"F0.wireOp",VERTEX,"E8.start");
            extrude(context, id + "F8", {"entities" : qUnion([Q0, Q1, Q2, Q3, Q4, Q5, Q6, Q7, Q8, Q9, Q10, Q11, Q12, Q13, Q14, Q15, Q16, Q17, Q18, Q19, Q20, Q21, Q22, Q23, Q24, Q25, Q26, Q27, Q28, Q29, Q30, Q31, Q32, Q33, Q34, Q35, Q36, Q37, Q38, Q39, Q40, Q41, Q42, Q43]), "endBound" : BoundingType.UP_TO_VERTEX, "depth" : 355.6 * mm, "endBoundEntityVertex" : qUnion([Q44]), "offsetDistance" : 25.4 * mm});
        }
        {
            var Q0;
            {var subQ0=sQuery(id+"F2.wireOp",EDGE,"E11.left");var subQ1=sQuery(id+"F2.wireOp",EDGE,"E11.bottom");var subQ2=makeQuery(id+"F2.imprint","INTERSECT",VERTEX,{"derivedFrom":[subQ1,subQ0]});Q0=makeQuery(id+"F2.imprint","IMPRINT",FACE,{"disambiguationData":[TD([[makeQuery(id+"F2.imprint","IMPRINT",EDGE,{"disambiguationData":[TD([[subQ2,-1.0]])],"derivedFrom":subQ1}),-1.0]])]});}
            var Q1;
            {var subQ0=sQuery(id+"F2.wireOp",EDGE,"E41.0.5.0");Q1=makeQuery(id+"F2.imprint","IMPRINT",FACE,{"disambiguationData":[TD([[makeQuery(id+"F2.imprint","IMPRINT",EDGE,{"derivedFrom":subQ0}),1.0]])]});}
            var Q2;
            {var subQ0=sQuery(id+"F2.wireOp",EDGE,"E41.0.4.0");Q2=makeQuery(id+"F2.imprint","IMPRINT",FACE,{"disambiguationData":[TD([[makeQuery(id+"F2.imprint","IMPRINT",EDGE,{"derivedFrom":subQ0}),1.0]])]});}
            var Q3;
            {var subQ0=sQuery(id+"F2.wireOp",EDGE,"E41.0.3.0");Q3=makeQuery(id+"F2.imprint","IMPRINT",FACE,{"disambiguationData":[TD([[makeQuery(id+"F2.imprint","IMPRINT",EDGE,{"derivedFrom":subQ0}),1.0]])]});}
            var Q4;
            {var subQ0=sQuery(id+"F2.wireOp",EDGE,"E41.0.2.0");Q4=makeQuery(id+"F2.imprint","IMPRINT",FACE,{"disambiguationData":[TD([[makeQuery(id+"F2.imprint","IMPRINT",EDGE,{"derivedFrom":subQ0}),1.0]])]});}
            var Q5;
            {var subQ0=sQuery(id+"F2.wireOp",EDGE,"E41.0.1.0");Q5=makeQuery(id+"F2.imprint","IMPRINT",FACE,{"disambiguationData":[TD([[makeQuery(id+"F2.imprint","IMPRINT",EDGE,{"derivedFrom":subQ0}),1.0]])]});}
            var Q6;
            {var subQ0=sQuery(id+"F2.wireOp",EDGE,"E39");Q6=makeQuery(id+"F2.imprint","IMPRINT",FACE,{"disambiguationData":[TD([[makeQuery(id+"F2.imprint","IMPRINT",EDGE,{"derivedFrom":subQ0}),1.0]])]});}
            var Q7;
            {var subQ0=sQuery(id+"F2.wireOp",EDGE,"E11.left");var subQ1=sQuery(id+"F2.wireOp",EDGE,"E11.top");var subQ2=makeQuery(id+"F2.imprint","INTERSECT",VERTEX,{"derivedFrom":[subQ1,subQ0]});Q7=makeQuery(id+"F2.imprint","IMPRINT",FACE,{"disambiguationData":[TD([[makeQuery(id+"F2.imprint","IMPRINT",EDGE,{"disambiguationData":[TD([[subQ2,-1.0]])],"derivedFrom":subQ1}),1.0]])]});}
            var Q8;
            Q8=sQuery(id+"F0.wireOp",VERTEX,"E10.start");
            extrude(context, id + "F9", {"entities" : qUnion([Q0, Q1, Q2, Q3, Q4, Q5, Q6, Q7]), "operationType" : NewBodyOperationType.ADD, "endBound" : BoundingType.UP_TO_VERTEX, "depth" : 25.4 * mm, "endBoundEntityVertex" : qUnion([Q8]), "offsetDistance" : 25.4 * mm});
        }
        {
            var Q0;
            {var subQ0=sQuery(id+"F6.wireOp",EDGE,"E75");var subQ1=sQuery(id+"F6.wireOp",EDGE,"E70.right");var subQ2=makeQuery(id+"F6.imprint","INTERSECT",VERTEX,{"derivedFrom":[subQ1,subQ0]});Q0=makeQuery(id+"F6.imprint","IMPRINT",FACE,{"disambiguationData":[TD([[makeQuery(id+"F6.imprint","IMPRINT",EDGE,{"disambiguationData":[TD([[subQ2,-1.0]])],"derivedFrom":subQ1}),-1.0]])]});}
            var Q1;
            {var subQ0=sQuery(id+"F6.wireOp",EDGE,"E74");var subQ1=sQuery(id+"F6.wireOp",EDGE,"E71");var subQ2=makeQuery(id+"F6.imprint","INTERSECT",VERTEX,{"derivedFrom":[subQ1,subQ0]});Q1=makeQuery(id+"F6.imprint","IMPRINT",FACE,{"disambiguationData":[TD([[makeQuery(id+"F6.imprint","IMPRINT",EDGE,{"disambiguationData":[TD([[subQ2,-1.0]])],"derivedFrom":subQ1}),-1.0]])]});}
            var Q2;
            {var subQ0=sQuery(id+"F6.wireOp",EDGE,"E75");var subQ1=sQuery(id+"F6.wireOp",EDGE,"E71");var subQ2=makeQuery(id+"F6.imprint","INTERSECT",VERTEX,{"derivedFrom":[subQ1,subQ0]});Q2=makeQuery(id+"F6.imprint","IMPRINT",FACE,{"disambiguationData":[TD([[makeQuery(id+"F6.imprint","IMPRINT",EDGE,{"disambiguationData":[TD([[subQ2,-1.0]])],"derivedFrom":subQ1}),-1.0]])]});}
            var Q3;
            {var subQ0=sQuery(id+"F6.wireOp",EDGE,"E75");var subQ1=sQuery(id+"F6.wireOp",EDGE,"E70.left");var subQ2=makeQuery(id+"F6.imprint","INTERSECT",VERTEX,{"derivedFrom":[subQ1,subQ0]});Q3=makeQuery(id+"F6.imprint","IMPRINT",FACE,{"disambiguationData":[TD([[makeQuery(id+"F6.imprint","IMPRINT",EDGE,{"disambiguationData":[TD([[subQ2,-1.0]])],"derivedFrom":subQ1}),1.0]])]});}
            var Q4;
            {var subQ0=sQuery(id+"F6.wireOp",EDGE,"E73");var subQ1=sQuery(id+"F6.wireOp",EDGE,"E71");var subQ2=makeQuery(id+"F6.imprint","INTERSECT",VERTEX,{"derivedFrom":[subQ1,subQ0]});Q4=makeQuery(id+"F6.imprint","IMPRINT",FACE,{"disambiguationData":[TD([[makeQuery(id+"F6.imprint","IMPRINT",EDGE,{"disambiguationData":[TD([[subQ2,1.0]])],"derivedFrom":subQ1}),-1.0]])]});}
            var Q5;
            {var subQ0=sQuery(id+"F6.wireOp",EDGE,"E70.right");var subQ1=sQuery(id+"F6.wireOp",EDGE,"E70.bottom");var subQ2=makeQuery(id+"F6.imprint","INTERSECT",VERTEX,{"derivedFrom":[subQ1,subQ0]});Q5=makeQuery(id+"F6.imprint","IMPRINT",FACE,{"disambiguationData":[TD([[makeQuery(id+"F6.imprint","IMPRINT",EDGE,{"disambiguationData":[TD([[subQ2,1.0]])],"derivedFrom":subQ1}),-1.0]])]});}
            var Q6;
            {var subQ0=sQuery(id+"F6.wireOp",EDGE,"E71");var subQ1=sQuery(id+"F6.wireOp",EDGE,"E70.bottom");var subQ2=makeQuery(id+"F6.imprint","INTERSECT",VERTEX,{"derivedFrom":[subQ1,subQ0]});Q6=makeQuery(id+"F6.imprint","IMPRINT",FACE,{"disambiguationData":[TD([[makeQuery(id+"F6.imprint","IMPRINT",EDGE,{"disambiguationData":[TD([[subQ2,1.0]])],"derivedFrom":subQ1}),-1.0]])]});}
            var Q7;
            {var subQ0=sQuery(id+"F6.wireOp",EDGE,"E70.left");var subQ1=sQuery(id+"F6.wireOp",EDGE,"E70.bottom");var subQ2=makeQuery(id+"F6.imprint","INTERSECT",VERTEX,{"derivedFrom":[subQ1,subQ0]});Q7=makeQuery(id+"F6.imprint","IMPRINT",FACE,{"disambiguationData":[TD([[makeQuery(id+"F6.imprint","IMPRINT",EDGE,{"disambiguationData":[TD([[subQ2,-1.0]])],"derivedFrom":subQ1}),-1.0]])]});}
            var Q8;
            {var subQ4=sQuery(id+"F6.wireOp",EDGE,"E70.top");Q8=makeQuery(id+"F6.imprint","IMPRINT",FACE,{"disambiguationData":[TD([[makeQuery(id+"F6.imprint","IMPRINT",EDGE,{"derivedFrom":subQ4}),1.0]])]});}
            var Q9;
            Q9=sQuery(id+"F0.wireOp",VERTEX,"E8.start");
            extrude(context, id + "F10", {"entities" : qUnion([Q0, Q1, Q2, Q3, Q4, Q5, Q6, Q7, Q8]), "operationType" : NewBodyOperationType.ADD, "endBound" : BoundingType.UP_TO_VERTEX, "oppositeDirection" : true, "depth" : 406.4 * mm, "endBoundEntityVertex" : qUnion([Q9]), "offsetDistance" : 25.4 * mm});
        }
        {
            var Q0;
            Q0=makeQuery(id+"F2.imprint","IMPRINT",FACE,{"disambiguationData":[TD([[makeQuery(id+"F2.imprint","IMPRINT",EDGE,{"derivedFrom":sQuery(id+"F2.wireOp",EDGE,"E32")}),1.0]])]});
            var Q1;
            Q1=makeQuery(id+"F2.imprint","IMPRINT",FACE,{"disambiguationData":[TD([[makeQuery(id+"F2.imprint","IMPRINT",EDGE,{"derivedFrom":sQuery(id+"F2.wireOp",EDGE,"E38")}),1.0]])]});
            var Q2;
            Q2=sQuery(id+"F0.wireOp",VERTEX,"E0.top.end");
            extrude(context, id + "F11", {"entities" : qUnion([Q0, Q1]), "operationType" : NewBodyOperationType.ADD, "endBound" : BoundingType.UP_TO_VERTEX, "depth" : 25.4 * mm, "endBoundEntityVertex" : qUnion([Q2]), "offsetDistance" : 25.4 * mm});
        }
        {
            var Q0;
            {var subQ0=sQuery(id+"F4.wireOp",EDGE,"E59.0.4.0");var subQ1=sQuery(id+"F4.wireOp",EDGE,"E46");var subQ2=makeQuery(id+"F4.imprint","INTERSECT",VERTEX,{"derivedFrom":[subQ1,subQ0]});Q0=makeQuery(id+"F4.imprint","IMPRINT",FACE,{"disambiguationData":[TD([[makeQuery(id+"F4.imprint","IMPRINT",EDGE,{"disambiguationData":[TD([[subQ2,-1.0]])],"derivedFrom":subQ1}),1.0]])]});}
            var Q1;
            {var subQ0=sQuery(id+"F4.wireOp",EDGE,"E59.0.3.1");var subQ1=sQuery(id+"F4.wireOp",EDGE,"E46");var subQ2=makeQuery(id+"F4.imprint","INTERSECT",VERTEX,{"derivedFrom":[subQ1,subQ0]});Q1=makeQuery(id+"F4.imprint","IMPRINT",FACE,{"disambiguationData":[TD([[makeQuery(id+"F4.imprint","IMPRINT",EDGE,{"disambiguationData":[TD([[subQ2,-1.0]])],"derivedFrom":subQ1}),1.0]])]});}
            var Q2;
            {var subQ0=sQuery(id+"F4.wireOp",EDGE,"E59.0.3.0");var subQ1=sQuery(id+"F4.wireOp",EDGE,"E46");var subQ2=makeQuery(id+"F4.imprint","INTERSECT",VERTEX,{"derivedFrom":[subQ1,subQ0]});Q2=makeQuery(id+"F4.imprint","IMPRINT",FACE,{"disambiguationData":[TD([[makeQuery(id+"F4.imprint","IMPRINT",EDGE,{"disambiguationData":[TD([[subQ2,-1.0]])],"derivedFrom":subQ1}),1.0]])]});}
            var Q3;
            {var subQ0=sQuery(id+"F4.wireOp",EDGE,"E59.0.2.1");var subQ1=sQuery(id+"F4.wireOp",EDGE,"E46");var subQ2=makeQuery(id+"F4.imprint","INTERSECT",VERTEX,{"derivedFrom":[subQ1,subQ0]});Q3=makeQuery(id+"F4.imprint","IMPRINT",FACE,{"disambiguationData":[TD([[makeQuery(id+"F4.imprint","IMPRINT",EDGE,{"disambiguationData":[TD([[subQ2,-1.0]])],"derivedFrom":subQ1}),1.0]])]});}
            var Q4;
            {var subQ0=sQuery(id+"F4.wireOp",EDGE,"E59.0.2.0");var subQ1=sQuery(id+"F4.wireOp",EDGE,"E46");var subQ2=makeQuery(id+"F4.imprint","INTERSECT",VERTEX,{"derivedFrom":[subQ1,subQ0]});Q4=makeQuery(id+"F4.imprint","IMPRINT",FACE,{"disambiguationData":[TD([[makeQuery(id+"F4.imprint","IMPRINT",EDGE,{"disambiguationData":[TD([[subQ2,-1.0]])],"derivedFrom":subQ1}),1.0]])]});}
            var Q5;
            {var subQ0=sQuery(id+"F4.wireOp",EDGE,"E59.0.1.1");var subQ1=sQuery(id+"F4.wireOp",EDGE,"E46");var subQ2=makeQuery(id+"F4.imprint","INTERSECT",VERTEX,{"derivedFrom":[subQ1,subQ0]});Q5=makeQuery(id+"F4.imprint","IMPRINT",FACE,{"disambiguationData":[TD([[makeQuery(id+"F4.imprint","IMPRINT",EDGE,{"disambiguationData":[TD([[subQ2,-1.0]])],"derivedFrom":subQ1}),1.0]])]});}
            var Q6;
            {var subQ0=sQuery(id+"F4.wireOp",EDGE,"E59.0.1.0");var subQ1=sQuery(id+"F4.wireOp",EDGE,"E46");var subQ2=makeQuery(id+"F4.imprint","INTERSECT",VERTEX,{"derivedFrom":[subQ1,subQ0]});Q6=makeQuery(id+"F4.imprint","IMPRINT",FACE,{"disambiguationData":[TD([[makeQuery(id+"F4.imprint","IMPRINT",EDGE,{"disambiguationData":[TD([[subQ2,-1.0]])],"derivedFrom":subQ1}),1.0]])]});}
            var Q7;
            {var subQ0=sQuery(id+"F4.wireOp",EDGE,"E55");var subQ1=sQuery(id+"F4.wireOp",EDGE,"E46");var subQ2=makeQuery(id+"F4.imprint","INTERSECT",VERTEX,{"derivedFrom":[subQ1,subQ0]});Q7=makeQuery(id+"F4.imprint","IMPRINT",FACE,{"disambiguationData":[TD([[makeQuery(id+"F4.imprint","IMPRINT",EDGE,{"disambiguationData":[TD([[subQ2,-1.0]])],"derivedFrom":subQ1}),1.0]])]});}
            var Q8;
            {var subQ0=sQuery(id+"F4.wireOp",EDGE,"E56");var subQ1=sQuery(id+"F4.wireOp",EDGE,"E46");var subQ2=makeQuery(id+"F4.imprint","INTERSECT",VERTEX,{"derivedFrom":[subQ1,subQ0]});Q8=makeQuery(id+"F4.imprint","IMPRINT",FACE,{"disambiguationData":[TD([[makeQuery(id+"F4.imprint","IMPRINT",EDGE,{"disambiguationData":[TD([[subQ2,-1.0]])],"derivedFrom":subQ1}),1.0]])]});}
            var Q9;
            {var subQ0=sQuery(id+"F4.wireOp",EDGE,"E60.0.2.1");var subQ1=sQuery(id+"F4.wireOp",EDGE,"E46");var subQ2=makeQuery(id+"F4.imprint","INTERSECT",VERTEX,{"derivedFrom":[subQ1,subQ0]});Q9=makeQuery(id+"F4.imprint","IMPRINT",FACE,{"disambiguationData":[TD([[makeQuery(id+"F4.imprint","IMPRINT",EDGE,{"disambiguationData":[TD([[subQ2,-1.0]])],"derivedFrom":subQ1}),1.0]])]});}
            var Q10;
            {var subQ0=sQuery(id+"F4.wireOp",EDGE,"E60.0.2.0");var subQ1=sQuery(id+"F4.wireOp",EDGE,"E46");var subQ2=makeQuery(id+"F4.imprint","INTERSECT",VERTEX,{"derivedFrom":[subQ1,subQ0]});Q10=makeQuery(id+"F4.imprint","IMPRINT",FACE,{"disambiguationData":[TD([[makeQuery(id+"F4.imprint","IMPRINT",EDGE,{"disambiguationData":[TD([[subQ2,-1.0]])],"derivedFrom":subQ1}),1.0]])]});}
            var Q11;
            {var subQ0=sQuery(id+"F4.wireOp",EDGE,"E60.0.1.1");var subQ1=sQuery(id+"F4.wireOp",EDGE,"E46");var subQ2=makeQuery(id+"F4.imprint","INTERSECT",VERTEX,{"derivedFrom":[subQ1,subQ0]});Q11=makeQuery(id+"F4.imprint","IMPRINT",FACE,{"disambiguationData":[TD([[makeQuery(id+"F4.imprint","IMPRINT",EDGE,{"disambiguationData":[TD([[subQ2,-1.0]])],"derivedFrom":subQ1}),1.0]])]});}
            var Q12;
            {var subQ0=sQuery(id+"F4.wireOp",EDGE,"E60.0.1.0");var subQ1=sQuery(id+"F4.wireOp",EDGE,"E46");var subQ2=makeQuery(id+"F4.imprint","INTERSECT",VERTEX,{"derivedFrom":[subQ1,subQ0]});Q12=makeQuery(id+"F4.imprint","IMPRINT",FACE,{"disambiguationData":[TD([[makeQuery(id+"F4.imprint","IMPRINT",EDGE,{"disambiguationData":[TD([[subQ2,-1.0]])],"derivedFrom":subQ1}),1.0]])]});}
            var Q13;
            {var subQ0=sQuery(id+"F4.wireOp",EDGE,"E58");var subQ1=sQuery(id+"F4.wireOp",EDGE,"E46");var subQ2=makeQuery(id+"F4.imprint","INTERSECT",VERTEX,{"derivedFrom":[subQ1,subQ0]});Q13=makeQuery(id+"F4.imprint","IMPRINT",FACE,{"disambiguationData":[TD([[makeQuery(id+"F4.imprint","IMPRINT",EDGE,{"disambiguationData":[TD([[subQ2,-1.0]])],"derivedFrom":subQ1}),1.0]])]});}
            var Q14;
            {var subQ0=sQuery(id+"F4.wireOp",EDGE,"E46");var subQ1=sQuery(id+"F4.wireOp",EDGE,"E45");var subQ2=makeQuery(id+"F4.imprint","INTERSECT",VERTEX,{"derivedFrom":[subQ1,subQ0]});Q14=makeQuery(id+"F4.imprint","IMPRINT",FACE,{"disambiguationData":[TD([[makeQuery(id+"F4.imprint","IMPRINT",EDGE,{"disambiguationData":[TD([[subQ2,1.0]])],"derivedFrom":subQ1}),-1.0]])]});}
            extrude(context, id + "F12", {"entities" : qUnion([Q0, Q1, Q2, Q3, Q4, Q5, Q6, Q7, Q8, Q9, Q10, Q11, Q12, Q13, Q14]), "depth" : 25.4 * mm, "offsetDistance" : 25.4 * mm});
        }
        {
            var Q0;
            {var subQ4=sQuery(id+"F4.wireOp",EDGE,"E43.top");Q0=makeQuery(id+"F4.imprint","IMPRINT",FACE,{"disambiguationData":[TD([[makeQuery(id+"F4.imprint","IMPRINT",EDGE,{"derivedFrom":subQ4}),-1.0]])]});}
            var Q1;
            {var subQ0=sQuery(id+"F4.wireOp",EDGE,"E46");var subQ1=sQuery(id+"F4.wireOp",EDGE,"E44");var subQ2=makeQuery(id+"F4.imprint","INTERSECT",VERTEX,{"derivedFrom":[subQ1,subQ0]});Q1=makeQuery(id+"F4.imprint","IMPRINT",FACE,{"disambiguationData":[TD([[makeQuery(id+"F4.imprint","IMPRINT",EDGE,{"disambiguationData":[TD([[subQ2,1.0]])],"derivedFrom":subQ1}),1.0]])]});}
            var Q2;
            {var subQ0=sQuery(id+"F4.wireOp",EDGE,"E63");var subQ1=sQuery(id+"F4.wireOp",EDGE,"E43.left");var subQ2=makeQuery(id+"F4.imprint","INTERSECT",VERTEX,{"derivedFrom":[subQ1,subQ0]});Q2=makeQuery(id+"F4.imprint","IMPRINT",FACE,{"disambiguationData":[TD([[makeQuery(id+"F4.imprint","IMPRINT",EDGE,{"disambiguationData":[TD([[subQ2,-1.0]])],"derivedFrom":subQ1}),-1.0]])]});}
            var Q3;
            {var subQ0=sQuery(id+"F4.wireOp",EDGE,"E64");var subQ1=sQuery(id+"F4.wireOp",EDGE,"E46");var subQ2=makeQuery(id+"F4.imprint","INTERSECT",VERTEX,{"derivedFrom":[subQ1,subQ0]});Q3=makeQuery(id+"F4.imprint","IMPRINT",FACE,{"disambiguationData":[TD([[makeQuery(id+"F4.imprint","IMPRINT",EDGE,{"disambiguationData":[TD([[subQ2,-1.0]])],"derivedFrom":subQ1}),1.0]])]});}
            var Q4;
            {var subQ0=sQuery(id+"F4.wireOp",EDGE,"E64");var subQ1=sQuery(id+"F4.wireOp",EDGE,"E47");var subQ2=makeQuery(id+"F4.imprint","INTERSECT",VERTEX,{"derivedFrom":[subQ1,subQ0]});Q4=makeQuery(id+"F4.imprint","IMPRINT",FACE,{"disambiguationData":[TD([[makeQuery(id+"F4.imprint","IMPRINT",EDGE,{"disambiguationData":[TD([[subQ2,-1.0]])],"derivedFrom":subQ1}),1.0]])]});}
            var Q5;
            {var subQ0=sQuery(id+"F4.wireOp",EDGE,"E63");var subQ1=sQuery(id+"F4.wireOp",EDGE,"E46");var subQ2=makeQuery(id+"F4.imprint","INTERSECT",VERTEX,{"derivedFrom":[subQ1,subQ0]});Q5=makeQuery(id+"F4.imprint","IMPRINT",FACE,{"disambiguationData":[TD([[makeQuery(id+"F4.imprint","IMPRINT",EDGE,{"disambiguationData":[TD([[subQ2,-1.0]])],"derivedFrom":subQ1}),1.0]])]});}
            var Q6;
            {var subQ0=sQuery(id+"F4.wireOp",EDGE,"E61");var subQ1=sQuery(id+"F4.wireOp",EDGE,"E43.left");var subQ2=makeQuery(id+"F4.imprint","INTERSECT",VERTEX,{"derivedFrom":[subQ1,subQ0]});Q6=makeQuery(id+"F4.imprint","IMPRINT",FACE,{"disambiguationData":[TD([[makeQuery(id+"F4.imprint","IMPRINT",EDGE,{"disambiguationData":[TD([[subQ2,-1.0]])],"derivedFrom":subQ1}),-1.0]])]});}
            var Q7;
            {var subQ0=sQuery(id+"F4.wireOp",EDGE,"E62");var subQ1=sQuery(id+"F4.wireOp",EDGE,"E46");var subQ2=makeQuery(id+"F4.imprint","INTERSECT",VERTEX,{"derivedFrom":[subQ1,subQ0]});Q7=makeQuery(id+"F4.imprint","IMPRINT",FACE,{"disambiguationData":[TD([[makeQuery(id+"F4.imprint","IMPRINT",EDGE,{"disambiguationData":[TD([[subQ2,-1.0]])],"derivedFrom":subQ1}),1.0]])]});}
            var Q8;
            {var subQ0=sQuery(id+"F4.wireOp",EDGE,"E62");var subQ1=sQuery(id+"F4.wireOp",EDGE,"E47");var subQ2=makeQuery(id+"F4.imprint","INTERSECT",VERTEX,{"derivedFrom":[subQ1,subQ0]});Q8=makeQuery(id+"F4.imprint","IMPRINT",FACE,{"disambiguationData":[TD([[makeQuery(id+"F4.imprint","IMPRINT",EDGE,{"disambiguationData":[TD([[subQ2,-1.0]])],"derivedFrom":subQ1}),1.0]])]});}
            var Q9;
            {var subQ0=sQuery(id+"F4.wireOp",EDGE,"E61");var subQ1=sQuery(id+"F4.wireOp",EDGE,"E46");var subQ2=makeQuery(id+"F4.imprint","INTERSECT",VERTEX,{"derivedFrom":[subQ1,subQ0]});Q9=makeQuery(id+"F4.imprint","IMPRINT",FACE,{"disambiguationData":[TD([[makeQuery(id+"F4.imprint","IMPRINT",EDGE,{"disambiguationData":[TD([[subQ2,-1.0]])],"derivedFrom":subQ1}),1.0]])]});}
            var Q10;
            {var subQ0=sQuery(id+"F4.wireOp",EDGE,"E59.0.4.0");var subQ1=sQuery(id+"F4.wireOp",EDGE,"E43.left");var subQ2=makeQuery(id+"F4.imprint","INTERSECT",VERTEX,{"derivedFrom":[subQ1,subQ0]});Q10=makeQuery(id+"F4.imprint","IMPRINT",FACE,{"disambiguationData":[TD([[makeQuery(id+"F4.imprint","IMPRINT",EDGE,{"disambiguationData":[TD([[subQ2,-1.0]])],"derivedFrom":subQ1}),-1.0]])]});}
            var Q11;
            {var subQ0=sQuery(id+"F4.wireOp",EDGE,"E59.0.4.1");var subQ1=sQuery(id+"F4.wireOp",EDGE,"E46");var subQ2=makeQuery(id+"F4.imprint","INTERSECT",VERTEX,{"derivedFrom":[subQ1,subQ0]});Q11=makeQuery(id+"F4.imprint","IMPRINT",FACE,{"disambiguationData":[TD([[makeQuery(id+"F4.imprint","IMPRINT",EDGE,{"disambiguationData":[TD([[subQ2,-1.0]])],"derivedFrom":subQ1}),1.0]])]});}
            var Q12;
            {var subQ0=sQuery(id+"F4.wireOp",EDGE,"E59.0.4.1");var subQ1=sQuery(id+"F4.wireOp",EDGE,"E47");var subQ2=makeQuery(id+"F4.imprint","INTERSECT",VERTEX,{"derivedFrom":[subQ1,subQ0]});Q12=makeQuery(id+"F4.imprint","IMPRINT",FACE,{"disambiguationData":[TD([[makeQuery(id+"F4.imprint","IMPRINT",EDGE,{"disambiguationData":[TD([[subQ2,-1.0]])],"derivedFrom":subQ1}),1.0]])]});}
            var Q13;
            {var subQ0=sQuery(id+"F4.wireOp",EDGE,"E59.0.4.0");var subQ1=sQuery(id+"F4.wireOp",EDGE,"E46");var subQ2=makeQuery(id+"F4.imprint","INTERSECT",VERTEX,{"derivedFrom":[subQ1,subQ0]});Q13=makeQuery(id+"F4.imprint","IMPRINT",FACE,{"disambiguationData":[TD([[makeQuery(id+"F4.imprint","IMPRINT",EDGE,{"disambiguationData":[TD([[subQ2,-1.0]])],"derivedFrom":subQ1}),1.0]])]});}
            var Q14;
            {var subQ0=sQuery(id+"F4.wireOp",EDGE,"E59.0.3.0");var subQ1=sQuery(id+"F4.wireOp",EDGE,"E43.left");var subQ2=makeQuery(id+"F4.imprint","INTERSECT",VERTEX,{"derivedFrom":[subQ1,subQ0]});Q14=makeQuery(id+"F4.imprint","IMPRINT",FACE,{"disambiguationData":[TD([[makeQuery(id+"F4.imprint","IMPRINT",EDGE,{"disambiguationData":[TD([[subQ2,-1.0]])],"derivedFrom":subQ1}),-1.0]])]});}
            var Q15;
            {var subQ0=sQuery(id+"F4.wireOp",EDGE,"E59.0.3.1");var subQ1=sQuery(id+"F4.wireOp",EDGE,"E46");var subQ2=makeQuery(id+"F4.imprint","INTERSECT",VERTEX,{"derivedFrom":[subQ1,subQ0]});Q15=makeQuery(id+"F4.imprint","IMPRINT",FACE,{"disambiguationData":[TD([[makeQuery(id+"F4.imprint","IMPRINT",EDGE,{"disambiguationData":[TD([[subQ2,-1.0]])],"derivedFrom":subQ1}),1.0]])]});}
            var Q16;
            {var subQ0=sQuery(id+"F4.wireOp",EDGE,"E59.0.3.1");var subQ1=sQuery(id+"F4.wireOp",EDGE,"E47");var subQ2=makeQuery(id+"F4.imprint","INTERSECT",VERTEX,{"derivedFrom":[subQ1,subQ0]});Q16=makeQuery(id+"F4.imprint","IMPRINT",FACE,{"disambiguationData":[TD([[makeQuery(id+"F4.imprint","IMPRINT",EDGE,{"disambiguationData":[TD([[subQ2,-1.0]])],"derivedFrom":subQ1}),1.0]])]});}
            var Q17;
            {var subQ0=sQuery(id+"F4.wireOp",EDGE,"E59.0.3.0");var subQ1=sQuery(id+"F4.wireOp",EDGE,"E46");var subQ2=makeQuery(id+"F4.imprint","INTERSECT",VERTEX,{"derivedFrom":[subQ1,subQ0]});Q17=makeQuery(id+"F4.imprint","IMPRINT",FACE,{"disambiguationData":[TD([[makeQuery(id+"F4.imprint","IMPRINT",EDGE,{"disambiguationData":[TD([[subQ2,-1.0]])],"derivedFrom":subQ1}),1.0]])]});}
            var Q18;
            {var subQ0=sQuery(id+"F4.wireOp",EDGE,"E59.0.2.1");var subQ1=sQuery(id+"F4.wireOp",EDGE,"E47");var subQ2=makeQuery(id+"F4.imprint","INTERSECT",VERTEX,{"derivedFrom":[subQ1,subQ0]});Q18=makeQuery(id+"F4.imprint","IMPRINT",FACE,{"disambiguationData":[TD([[makeQuery(id+"F4.imprint","IMPRINT",EDGE,{"disambiguationData":[TD([[subQ2,-1.0]])],"derivedFrom":subQ1}),1.0]])]});}
            var Q19;
            {var subQ0=sQuery(id+"F4.wireOp",EDGE,"E59.0.2.1");var subQ1=sQuery(id+"F4.wireOp",EDGE,"E46");var subQ2=makeQuery(id+"F4.imprint","INTERSECT",VERTEX,{"derivedFrom":[subQ1,subQ0]});Q19=makeQuery(id+"F4.imprint","IMPRINT",FACE,{"disambiguationData":[TD([[makeQuery(id+"F4.imprint","IMPRINT",EDGE,{"disambiguationData":[TD([[subQ2,-1.0]])],"derivedFrom":subQ1}),1.0]])]});}
            var Q20;
            {var subQ0=sQuery(id+"F4.wireOp",EDGE,"E59.0.2.0");var subQ1=sQuery(id+"F4.wireOp",EDGE,"E43.left");var subQ2=makeQuery(id+"F4.imprint","INTERSECT",VERTEX,{"derivedFrom":[subQ1,subQ0]});Q20=makeQuery(id+"F4.imprint","IMPRINT",FACE,{"disambiguationData":[TD([[makeQuery(id+"F4.imprint","IMPRINT",EDGE,{"disambiguationData":[TD([[subQ2,-1.0]])],"derivedFrom":subQ1}),-1.0]])]});}
            var Q21;
            {var subQ0=sQuery(id+"F4.wireOp",EDGE,"E59.0.2.0");var subQ1=sQuery(id+"F4.wireOp",EDGE,"E46");var subQ2=makeQuery(id+"F4.imprint","INTERSECT",VERTEX,{"derivedFrom":[subQ1,subQ0]});Q21=makeQuery(id+"F4.imprint","IMPRINT",FACE,{"disambiguationData":[TD([[makeQuery(id+"F4.imprint","IMPRINT",EDGE,{"disambiguationData":[TD([[subQ2,-1.0]])],"derivedFrom":subQ1}),1.0]])]});}
            var Q22;
            {var subQ0=sQuery(id+"F4.wireOp",EDGE,"E59.0.1.1");var subQ1=sQuery(id+"F4.wireOp",EDGE,"E47");var subQ2=makeQuery(id+"F4.imprint","INTERSECT",VERTEX,{"derivedFrom":[subQ1,subQ0]});Q22=makeQuery(id+"F4.imprint","IMPRINT",FACE,{"disambiguationData":[TD([[makeQuery(id+"F4.imprint","IMPRINT",EDGE,{"disambiguationData":[TD([[subQ2,-1.0]])],"derivedFrom":subQ1}),1.0]])]});}
            var Q23;
            {var subQ0=sQuery(id+"F4.wireOp",EDGE,"E59.0.1.1");var subQ1=sQuery(id+"F4.wireOp",EDGE,"E46");var subQ2=makeQuery(id+"F4.imprint","INTERSECT",VERTEX,{"derivedFrom":[subQ1,subQ0]});Q23=makeQuery(id+"F4.imprint","IMPRINT",FACE,{"disambiguationData":[TD([[makeQuery(id+"F4.imprint","IMPRINT",EDGE,{"disambiguationData":[TD([[subQ2,-1.0]])],"derivedFrom":subQ1}),1.0]])]});}
            var Q24;
            {var subQ0=sQuery(id+"F4.wireOp",EDGE,"E59.0.1.0");var subQ1=sQuery(id+"F4.wireOp",EDGE,"E43.left");var subQ2=makeQuery(id+"F4.imprint","INTERSECT",VERTEX,{"derivedFrom":[subQ1,subQ0]});Q24=makeQuery(id+"F4.imprint","IMPRINT",FACE,{"disambiguationData":[TD([[makeQuery(id+"F4.imprint","IMPRINT",EDGE,{"disambiguationData":[TD([[subQ2,-1.0]])],"derivedFrom":subQ1}),-1.0]])]});}
            var Q25;
            {var subQ0=sQuery(id+"F4.wireOp",EDGE,"E59.0.1.0");var subQ1=sQuery(id+"F4.wireOp",EDGE,"E46");var subQ2=makeQuery(id+"F4.imprint","INTERSECT",VERTEX,{"derivedFrom":[subQ1,subQ0]});Q25=makeQuery(id+"F4.imprint","IMPRINT",FACE,{"disambiguationData":[TD([[makeQuery(id+"F4.imprint","IMPRINT",EDGE,{"disambiguationData":[TD([[subQ2,-1.0]])],"derivedFrom":subQ1}),1.0]])]});}
            var Q26;
            {var subQ0=sQuery(id+"F4.wireOp",EDGE,"E55");var subQ1=sQuery(id+"F4.wireOp",EDGE,"E47");var subQ2=makeQuery(id+"F4.imprint","INTERSECT",VERTEX,{"derivedFrom":[subQ1,subQ0]});Q26=makeQuery(id+"F4.imprint","IMPRINT",FACE,{"disambiguationData":[TD([[makeQuery(id+"F4.imprint","IMPRINT",EDGE,{"disambiguationData":[TD([[subQ2,-1.0]])],"derivedFrom":subQ1}),1.0]])]});}
            var Q27;
            {var subQ0=sQuery(id+"F4.wireOp",EDGE,"E55");var subQ1=sQuery(id+"F4.wireOp",EDGE,"E46");var subQ2=makeQuery(id+"F4.imprint","INTERSECT",VERTEX,{"derivedFrom":[subQ1,subQ0]});Q27=makeQuery(id+"F4.imprint","IMPRINT",FACE,{"disambiguationData":[TD([[makeQuery(id+"F4.imprint","IMPRINT",EDGE,{"disambiguationData":[TD([[subQ2,-1.0]])],"derivedFrom":subQ1}),1.0]])]});}
            var Q28;
            {var subQ0=sQuery(id+"F4.wireOp",EDGE,"E55");var subQ1=sQuery(id+"F4.wireOp",EDGE,"E43.left");var subQ2=makeQuery(id+"F4.imprint","INTERSECT",VERTEX,{"derivedFrom":[subQ1,subQ0]});Q28=makeQuery(id+"F4.imprint","IMPRINT",FACE,{"disambiguationData":[TD([[makeQuery(id+"F4.imprint","IMPRINT",EDGE,{"disambiguationData":[TD([[subQ2,1.0]])],"derivedFrom":subQ1}),-1.0]])]});}
            var Q29;
            {var subQ0=sQuery(id+"F4.wireOp",EDGE,"E56");var subQ1=sQuery(id+"F4.wireOp",EDGE,"E46");var subQ2=makeQuery(id+"F4.imprint","INTERSECT",VERTEX,{"derivedFrom":[subQ1,subQ0]});Q29=makeQuery(id+"F4.imprint","IMPRINT",FACE,{"disambiguationData":[TD([[makeQuery(id+"F4.imprint","IMPRINT",EDGE,{"disambiguationData":[TD([[subQ2,-1.0]])],"derivedFrom":subQ1}),1.0]])]});}
            var Q30;
            {var subQ0=sQuery(id+"F4.wireOp",EDGE,"E60.0.2.1");var subQ1=sQuery(id+"F4.wireOp",EDGE,"E47");var subQ2=makeQuery(id+"F4.imprint","INTERSECT",VERTEX,{"derivedFrom":[subQ1,subQ0]});Q30=makeQuery(id+"F4.imprint","IMPRINT",FACE,{"disambiguationData":[TD([[makeQuery(id+"F4.imprint","IMPRINT",EDGE,{"disambiguationData":[TD([[subQ2,-1.0]])],"derivedFrom":subQ1}),1.0]])]});}
            var Q31;
            {var subQ0=sQuery(id+"F4.wireOp",EDGE,"E60.0.2.1");var subQ1=sQuery(id+"F4.wireOp",EDGE,"E46");var subQ2=makeQuery(id+"F4.imprint","INTERSECT",VERTEX,{"derivedFrom":[subQ1,subQ0]});Q31=makeQuery(id+"F4.imprint","IMPRINT",FACE,{"disambiguationData":[TD([[makeQuery(id+"F4.imprint","IMPRINT",EDGE,{"disambiguationData":[TD([[subQ2,-1.0]])],"derivedFrom":subQ1}),1.0]])]});}
            var Q32;
            {var subQ0=sQuery(id+"F4.wireOp",EDGE,"E60.0.2.0");var subQ1=sQuery(id+"F4.wireOp",EDGE,"E43.left");var subQ2=makeQuery(id+"F4.imprint","INTERSECT",VERTEX,{"derivedFrom":[subQ1,subQ0]});Q32=makeQuery(id+"F4.imprint","IMPRINT",FACE,{"disambiguationData":[TD([[makeQuery(id+"F4.imprint","IMPRINT",EDGE,{"disambiguationData":[TD([[subQ2,-1.0]])],"derivedFrom":subQ1}),-1.0]])]});}
            var Q33;
            {var subQ0=sQuery(id+"F4.wireOp",EDGE,"E60.0.2.0");var subQ1=sQuery(id+"F4.wireOp",EDGE,"E46");var subQ2=makeQuery(id+"F4.imprint","INTERSECT",VERTEX,{"derivedFrom":[subQ1,subQ0]});Q33=makeQuery(id+"F4.imprint","IMPRINT",FACE,{"disambiguationData":[TD([[makeQuery(id+"F4.imprint","IMPRINT",EDGE,{"disambiguationData":[TD([[subQ2,-1.0]])],"derivedFrom":subQ1}),1.0]])]});}
            var Q34;
            {var subQ0=sQuery(id+"F4.wireOp",EDGE,"E60.0.1.1");var subQ1=sQuery(id+"F4.wireOp",EDGE,"E47");var subQ2=makeQuery(id+"F4.imprint","INTERSECT",VERTEX,{"derivedFrom":[subQ1,subQ0]});Q34=makeQuery(id+"F4.imprint","IMPRINT",FACE,{"disambiguationData":[TD([[makeQuery(id+"F4.imprint","IMPRINT",EDGE,{"disambiguationData":[TD([[subQ2,-1.0]])],"derivedFrom":subQ1}),1.0]])]});}
            var Q35;
            {var subQ0=sQuery(id+"F4.wireOp",EDGE,"E60.0.1.1");var subQ1=sQuery(id+"F4.wireOp",EDGE,"E46");var subQ2=makeQuery(id+"F4.imprint","INTERSECT",VERTEX,{"derivedFrom":[subQ1,subQ0]});Q35=makeQuery(id+"F4.imprint","IMPRINT",FACE,{"disambiguationData":[TD([[makeQuery(id+"F4.imprint","IMPRINT",EDGE,{"disambiguationData":[TD([[subQ2,-1.0]])],"derivedFrom":subQ1}),1.0]])]});}
            var Q36;
            {var subQ0=sQuery(id+"F4.wireOp",EDGE,"E60.0.1.0");var subQ1=sQuery(id+"F4.wireOp",EDGE,"E43.left");var subQ2=makeQuery(id+"F4.imprint","INTERSECT",VERTEX,{"derivedFrom":[subQ1,subQ0]});Q36=makeQuery(id+"F4.imprint","IMPRINT",FACE,{"disambiguationData":[TD([[makeQuery(id+"F4.imprint","IMPRINT",EDGE,{"disambiguationData":[TD([[subQ2,-1.0]])],"derivedFrom":subQ1}),-1.0]])]});}
            var Q37;
            {var subQ0=sQuery(id+"F4.wireOp",EDGE,"E60.0.1.0");var subQ1=sQuery(id+"F4.wireOp",EDGE,"E46");var subQ2=makeQuery(id+"F4.imprint","INTERSECT",VERTEX,{"derivedFrom":[subQ1,subQ0]});Q37=makeQuery(id+"F4.imprint","IMPRINT",FACE,{"disambiguationData":[TD([[makeQuery(id+"F4.imprint","IMPRINT",EDGE,{"disambiguationData":[TD([[subQ2,-1.0]])],"derivedFrom":subQ1}),1.0]])]});}
            var Q38;
            {var subQ0=sQuery(id+"F4.wireOp",EDGE,"E58");var subQ1=sQuery(id+"F4.wireOp",EDGE,"E47");var subQ2=makeQuery(id+"F4.imprint","INTERSECT",VERTEX,{"derivedFrom":[subQ1,subQ0]});Q38=makeQuery(id+"F4.imprint","IMPRINT",FACE,{"disambiguationData":[TD([[makeQuery(id+"F4.imprint","IMPRINT",EDGE,{"disambiguationData":[TD([[subQ2,-1.0]])],"derivedFrom":subQ1}),1.0]])]});}
            var Q39;
            {var subQ0=sQuery(id+"F4.wireOp",EDGE,"E58");var subQ1=sQuery(id+"F4.wireOp",EDGE,"E46");var subQ2=makeQuery(id+"F4.imprint","INTERSECT",VERTEX,{"derivedFrom":[subQ1,subQ0]});Q39=makeQuery(id+"F4.imprint","IMPRINT",FACE,{"disambiguationData":[TD([[makeQuery(id+"F4.imprint","IMPRINT",EDGE,{"disambiguationData":[TD([[subQ2,-1.0]])],"derivedFrom":subQ1}),1.0]])]});}
            var Q40;
            {var subQ0=sQuery(id+"F4.wireOp",EDGE,"E57");var subQ1=sQuery(id+"F4.wireOp",EDGE,"E43.left");var subQ2=makeQuery(id+"F4.imprint","INTERSECT",VERTEX,{"derivedFrom":[subQ1,subQ0]});Q40=makeQuery(id+"F4.imprint","IMPRINT",FACE,{"disambiguationData":[TD([[makeQuery(id+"F4.imprint","IMPRINT",EDGE,{"disambiguationData":[TD([[subQ2,-1.0]])],"derivedFrom":subQ1}),-1.0]])]});}
            var Q41;
            {var subQ0=sQuery(id+"F4.wireOp",EDGE,"E46");var subQ1=sQuery(id+"F4.wireOp",EDGE,"E45");var subQ2=makeQuery(id+"F4.imprint","INTERSECT",VERTEX,{"derivedFrom":[subQ1,subQ0]});Q41=makeQuery(id+"F4.imprint","IMPRINT",FACE,{"disambiguationData":[TD([[makeQuery(id+"F4.imprint","IMPRINT",EDGE,{"disambiguationData":[TD([[subQ2,1.0]])],"derivedFrom":subQ1}),-1.0]])]});}
            var Q42;
            {var subQ4=sQuery(id+"F4.wireOp",EDGE,"E43.bottom");Q42=makeQuery(id+"F4.imprint","IMPRINT",FACE,{"disambiguationData":[TD([[makeQuery(id+"F4.imprint","IMPRINT",EDGE,{"derivedFrom":subQ4}),1.0]])]});}
            var Q43;
            {var subQ18=sQuery(id+"F4.wireOp",EDGE,"E49");Q43=makeQuery(id+"F4.imprint","IMPRINT",FACE,{"disambiguationData":[TD([[makeQuery(id+"F4.imprint","IMPRINT",EDGE,{"derivedFrom":subQ18}),-1.0]])]});}
            var Q44;
            Q44=sQuery(id+"F0.wireOp",VERTEX,"E5.start");
            extrude(context, id + "F13", {"entities" : qUnion([Q0, Q1, Q2, Q3, Q4, Q5, Q6, Q7, Q8, Q9, Q10, Q11, Q12, Q13, Q14, Q15, Q16, Q17, Q18, Q19, Q20, Q21, Q22, Q23, Q24, Q25, Q26, Q27, Q28, Q29, Q30, Q31, Q32, Q33, Q34, Q35, Q36, Q37, Q38, Q39, Q40, Q41, Q42, Q43]), "operationType" : NewBodyOperationType.ADD, "endBound" : BoundingType.UP_TO_VERTEX, "depth" : 355.6 * mm, "endBoundEntityVertex" : qUnion([Q44]), "offsetDistance" : 25.4 * mm});
        }
        {
            var Q0;
            {var subQ0=sQuery(id+"F0.wireOp",EDGE,"E6");Q0=makeQuery(id+"F0.imprint","IMPRINT",FACE,{"disambiguationData":[TD([[makeQuery(id+"F0.imprint","IMPRINT",EDGE,{"derivedFrom":subQ0}),-1.0]])]});}
            var Q1;
            Q1=sQuery(id+"F4.wireOp",VERTEX,"E43.right.end");
            extrude(context, id + "F14", {"entities" : qUnion([Q0]), "operationType" : NewBodyOperationType.REMOVE, "endBound" : BoundingType.UP_TO_VERTEX, "depth" : 25.4 * mm, "endBoundEntityVertex" : qUnion([Q1]), "offsetDistance" : 25.4 * mm});
        }
        {
            var Q0;
            {var subQ0=sQuery(id+"F2.wireOp",EDGE,"E13");var subQ1=sQuery(id+"F2.wireOp",EDGE,"E12");var subQ2=makeQuery(id+"F2.imprint","INTERSECT",VERTEX,{"derivedFrom":[subQ1,subQ0]});Q0=makeQuery(id+"F2.imprint","IMPRINT",FACE,{"disambiguationData":[TD([[makeQuery(id+"F2.imprint","IMPRINT",EDGE,{"disambiguationData":[TD([[subQ2,1.0]])],"derivedFrom":subQ1}),1.0]])]});}
            var Q1;
            {var subQ0=sQuery(id+"F2.wireOp",EDGE,"E14");var subQ1=sQuery(id+"F2.wireOp",EDGE,"E12");var subQ2=makeQuery(id+"F2.imprint","INTERSECT",VERTEX,{"derivedFrom":[subQ1,subQ0]});Q1=makeQuery(id+"F2.imprint","IMPRINT",FACE,{"disambiguationData":[TD([[makeQuery(id+"F2.imprint","IMPRINT",EDGE,{"disambiguationData":[TD([[subQ2,-1.0]])],"derivedFrom":subQ1}),1.0]])]});}
            var Q2;
            {var subQ0=sQuery(id+"F2.wireOp",EDGE,"E25");var subQ1=sQuery(id+"F2.wireOp",EDGE,"E13");var subQ2=makeQuery(id+"F2.imprint","INTERSECT",VERTEX,{"derivedFrom":[subQ1,subQ0]});Q2=makeQuery(id+"F2.imprint","IMPRINT",FACE,{"disambiguationData":[TD([[makeQuery(id+"F2.imprint","IMPRINT",EDGE,{"disambiguationData":[TD([[subQ2,-1.0]])],"derivedFrom":subQ1}),1.0]])]});}
            var Q3;
            {var subQ0=sQuery(id+"F2.wireOp",EDGE,"E25");var subQ1=sQuery(id+"F2.wireOp",EDGE,"E14");var subQ2=makeQuery(id+"F2.imprint","INTERSECT",VERTEX,{"derivedFrom":[subQ1,subQ0]});Q3=makeQuery(id+"F2.imprint","IMPRINT",FACE,{"disambiguationData":[TD([[makeQuery(id+"F2.imprint","IMPRINT",EDGE,{"disambiguationData":[TD([[subQ2,-1.0]])],"derivedFrom":subQ1}),-1.0]])]});}
            var Q4;
            {var subQ0=sQuery(id+"F2.wireOp",EDGE,"E26.0.1.1");var subQ1=sQuery(id+"F2.wireOp",EDGE,"E13");var subQ2=makeQuery(id+"F2.imprint","INTERSECT",VERTEX,{"derivedFrom":[subQ1,subQ0]});Q4=makeQuery(id+"F2.imprint","IMPRINT",FACE,{"disambiguationData":[TD([[makeQuery(id+"F2.imprint","IMPRINT",EDGE,{"disambiguationData":[TD([[subQ2,-1.0]])],"derivedFrom":subQ1}),1.0]])]});}
            var Q5;
            {var subQ0=sQuery(id+"F2.wireOp",EDGE,"E26.0.1.1");var subQ1=sQuery(id+"F2.wireOp",EDGE,"E14");var subQ2=makeQuery(id+"F2.imprint","INTERSECT",VERTEX,{"derivedFrom":[subQ1,subQ0]});Q5=makeQuery(id+"F2.imprint","IMPRINT",FACE,{"disambiguationData":[TD([[makeQuery(id+"F2.imprint","IMPRINT",EDGE,{"disambiguationData":[TD([[subQ2,-1.0]])],"derivedFrom":subQ1}),-1.0]])]});}
            var Q6;
            {var subQ0=sQuery(id+"F2.wireOp",EDGE,"E26.0.2.1");var subQ1=sQuery(id+"F2.wireOp",EDGE,"E13");var subQ2=makeQuery(id+"F2.imprint","INTERSECT",VERTEX,{"derivedFrom":[subQ1,subQ0]});Q6=makeQuery(id+"F2.imprint","IMPRINT",FACE,{"disambiguationData":[TD([[makeQuery(id+"F2.imprint","IMPRINT",EDGE,{"disambiguationData":[TD([[subQ2,-1.0]])],"derivedFrom":subQ1}),1.0]])]});}
            var Q7;
            {var subQ0=sQuery(id+"F2.wireOp",EDGE,"E26.0.2.1");var subQ1=sQuery(id+"F2.wireOp",EDGE,"E14");var subQ2=makeQuery(id+"F2.imprint","INTERSECT",VERTEX,{"derivedFrom":[subQ1,subQ0]});Q7=makeQuery(id+"F2.imprint","IMPRINT",FACE,{"disambiguationData":[TD([[makeQuery(id+"F2.imprint","IMPRINT",EDGE,{"disambiguationData":[TD([[subQ2,-1.0]])],"derivedFrom":subQ1}),-1.0]])]});}
            var Q8;
            {var subQ0=sQuery(id+"F2.wireOp",EDGE,"E26.0.3.1");var subQ1=sQuery(id+"F2.wireOp",EDGE,"E13");var subQ2=makeQuery(id+"F2.imprint","INTERSECT",VERTEX,{"derivedFrom":[subQ1,subQ0]});Q8=makeQuery(id+"F2.imprint","IMPRINT",FACE,{"disambiguationData":[TD([[makeQuery(id+"F2.imprint","IMPRINT",EDGE,{"disambiguationData":[TD([[subQ2,-1.0]])],"derivedFrom":subQ1}),1.0]])]});}
            var Q9;
            {var subQ0=sQuery(id+"F2.wireOp",EDGE,"E26.0.3.1");var subQ1=sQuery(id+"F2.wireOp",EDGE,"E14");var subQ2=makeQuery(id+"F2.imprint","INTERSECT",VERTEX,{"derivedFrom":[subQ1,subQ0]});Q9=makeQuery(id+"F2.imprint","IMPRINT",FACE,{"disambiguationData":[TD([[makeQuery(id+"F2.imprint","IMPRINT",EDGE,{"disambiguationData":[TD([[subQ2,-1.0]])],"derivedFrom":subQ1}),-1.0]])]});}
            var Q10;
            {var subQ0=sQuery(id+"F2.wireOp",EDGE,"E26.0.4.1");var subQ1=sQuery(id+"F2.wireOp",EDGE,"E13");var subQ2=makeQuery(id+"F2.imprint","INTERSECT",VERTEX,{"derivedFrom":[subQ1,subQ0]});Q10=makeQuery(id+"F2.imprint","IMPRINT",FACE,{"disambiguationData":[TD([[makeQuery(id+"F2.imprint","IMPRINT",EDGE,{"disambiguationData":[TD([[subQ2,-1.0]])],"derivedFrom":subQ1}),1.0]])]});}
            var Q11;
            {var subQ0=sQuery(id+"F2.wireOp",EDGE,"E26.0.4.1");var subQ1=sQuery(id+"F2.wireOp",EDGE,"E14");var subQ2=makeQuery(id+"F2.imprint","INTERSECT",VERTEX,{"derivedFrom":[subQ1,subQ0]});Q11=makeQuery(id+"F2.imprint","IMPRINT",FACE,{"disambiguationData":[TD([[makeQuery(id+"F2.imprint","IMPRINT",EDGE,{"disambiguationData":[TD([[subQ2,-1.0]])],"derivedFrom":subQ1}),-1.0]])]});}
            var Q12;
            Q12=sQuery(id+"F0.wireOp",VERTEX,"E8.start");
            extrude(context, id + "F15", {"entities" : qUnion([Q0, Q1, Q2, Q3, Q4, Q5, Q6, Q7, Q8, Q9, Q10, Q11]), "operationType" : NewBodyOperationType.ADD, "endBound" : BoundingType.UP_TO_VERTEX, "depth" : 25.4 * mm, "endBoundEntityVertex" : qUnion([Q12]), "hasOffset" : true, "offsetDistance" : 12.7 * mm, "offsetOppositeDirection" : true});
        }
        {
            var Q0;
            {var subQ0=sQuery(id+"F4.wireOp",EDGE,"E59.0.3.1");var subQ1=sQuery(id+"F4.wireOp",EDGE,"E43.left");var subQ2=makeQuery(id+"F4.imprint","INTERSECT",VERTEX,{"derivedFrom":[subQ1,subQ0]});Q0=makeQuery(id+"F4.imprint","IMPRINT",FACE,{"disambiguationData":[TD([[makeQuery(id+"F4.imprint","IMPRINT",EDGE,{"disambiguationData":[TD([[subQ2,-1.0]])],"derivedFrom":subQ1}),-1.0]])]});}
            var Q1;
            {var subQ0=sQuery(id+"F4.wireOp",EDGE,"E59.0.4.0");var subQ1=sQuery(id+"F4.wireOp",EDGE,"E47");var subQ2=makeQuery(id+"F4.imprint","INTERSECT",VERTEX,{"derivedFrom":[subQ1,subQ0]});Q1=makeQuery(id+"F4.imprint","IMPRINT",FACE,{"disambiguationData":[TD([[makeQuery(id+"F4.imprint","IMPRINT",EDGE,{"disambiguationData":[TD([[subQ2,-1.0]])],"derivedFrom":subQ1}),1.0]])]});}
            var Q2;
            {var subQ0=sQuery(id+"F4.wireOp",EDGE,"E59.0.2.1");var subQ1=sQuery(id+"F4.wireOp",EDGE,"E43.left");var subQ2=makeQuery(id+"F4.imprint","INTERSECT",VERTEX,{"derivedFrom":[subQ1,subQ0]});Q2=makeQuery(id+"F4.imprint","IMPRINT",FACE,{"disambiguationData":[TD([[makeQuery(id+"F4.imprint","IMPRINT",EDGE,{"disambiguationData":[TD([[subQ2,-1.0]])],"derivedFrom":subQ1}),-1.0]])]});}
            var Q3;
            {var subQ0=sQuery(id+"F4.wireOp",EDGE,"E59.0.3.0");var subQ1=sQuery(id+"F4.wireOp",EDGE,"E47");var subQ2=makeQuery(id+"F4.imprint","INTERSECT",VERTEX,{"derivedFrom":[subQ1,subQ0]});Q3=makeQuery(id+"F4.imprint","IMPRINT",FACE,{"disambiguationData":[TD([[makeQuery(id+"F4.imprint","IMPRINT",EDGE,{"disambiguationData":[TD([[subQ2,-1.0]])],"derivedFrom":subQ1}),1.0]])]});}
            var Q4;
            {var subQ0=sQuery(id+"F4.wireOp",EDGE,"E59.0.1.1");var subQ1=sQuery(id+"F4.wireOp",EDGE,"E43.left");var subQ2=makeQuery(id+"F4.imprint","INTERSECT",VERTEX,{"derivedFrom":[subQ1,subQ0]});Q4=makeQuery(id+"F4.imprint","IMPRINT",FACE,{"disambiguationData":[TD([[makeQuery(id+"F4.imprint","IMPRINT",EDGE,{"disambiguationData":[TD([[subQ2,-1.0]])],"derivedFrom":subQ1}),-1.0]])]});}
            var Q5;
            {var subQ0=sQuery(id+"F4.wireOp",EDGE,"E59.0.2.0");var subQ1=sQuery(id+"F4.wireOp",EDGE,"E47");var subQ2=makeQuery(id+"F4.imprint","INTERSECT",VERTEX,{"derivedFrom":[subQ1,subQ0]});Q5=makeQuery(id+"F4.imprint","IMPRINT",FACE,{"disambiguationData":[TD([[makeQuery(id+"F4.imprint","IMPRINT",EDGE,{"disambiguationData":[TD([[subQ2,-1.0]])],"derivedFrom":subQ1}),1.0]])]});}
            var Q6;
            {var subQ0=sQuery(id+"F4.wireOp",EDGE,"E55");var subQ1=sQuery(id+"F4.wireOp",EDGE,"E43.left");var subQ2=makeQuery(id+"F4.imprint","INTERSECT",VERTEX,{"derivedFrom":[subQ1,subQ0]});Q6=makeQuery(id+"F4.imprint","IMPRINT",FACE,{"disambiguationData":[TD([[makeQuery(id+"F4.imprint","IMPRINT",EDGE,{"disambiguationData":[TD([[subQ2,-1.0]])],"derivedFrom":subQ1}),-1.0]])]});}
            var Q7;
            {var subQ0=sQuery(id+"F4.wireOp",EDGE,"E59.0.1.0");var subQ1=sQuery(id+"F4.wireOp",EDGE,"E47");var subQ2=makeQuery(id+"F4.imprint","INTERSECT",VERTEX,{"derivedFrom":[subQ1,subQ0]});Q7=makeQuery(id+"F4.imprint","IMPRINT",FACE,{"disambiguationData":[TD([[makeQuery(id+"F4.imprint","IMPRINT",EDGE,{"disambiguationData":[TD([[subQ2,-1.0]])],"derivedFrom":subQ1}),1.0]])]});}
            var Q8;
            {var subQ0=sQuery(id+"F4.wireOp",EDGE,"E56");var subQ1=sQuery(id+"F4.wireOp",EDGE,"E43.left");var subQ2=makeQuery(id+"F4.imprint","INTERSECT",VERTEX,{"derivedFrom":[subQ1,subQ0]});Q8=makeQuery(id+"F4.imprint","IMPRINT",FACE,{"disambiguationData":[TD([[makeQuery(id+"F4.imprint","IMPRINT",EDGE,{"disambiguationData":[TD([[subQ2,1.0]])],"derivedFrom":subQ1}),-1.0]])]});}
            var Q9;
            {var subQ0=sQuery(id+"F4.wireOp",EDGE,"E56");var subQ1=sQuery(id+"F4.wireOp",EDGE,"E47");var subQ2=makeQuery(id+"F4.imprint","INTERSECT",VERTEX,{"derivedFrom":[subQ1,subQ0]});Q9=makeQuery(id+"F4.imprint","IMPRINT",FACE,{"disambiguationData":[TD([[makeQuery(id+"F4.imprint","IMPRINT",EDGE,{"disambiguationData":[TD([[subQ2,-1.0]])],"derivedFrom":subQ1}),1.0]])]});}
            var Q10;
            {var subQ0=sQuery(id+"F4.wireOp",EDGE,"E60.0.1.1");var subQ1=sQuery(id+"F4.wireOp",EDGE,"E43.left");var subQ2=makeQuery(id+"F4.imprint","INTERSECT",VERTEX,{"derivedFrom":[subQ1,subQ0]});Q10=makeQuery(id+"F4.imprint","IMPRINT",FACE,{"disambiguationData":[TD([[makeQuery(id+"F4.imprint","IMPRINT",EDGE,{"disambiguationData":[TD([[subQ2,-1.0]])],"derivedFrom":subQ1}),-1.0]])]});}
            var Q11;
            {var subQ0=sQuery(id+"F4.wireOp",EDGE,"E60.0.2.0");var subQ1=sQuery(id+"F4.wireOp",EDGE,"E47");var subQ2=makeQuery(id+"F4.imprint","INTERSECT",VERTEX,{"derivedFrom":[subQ1,subQ0]});Q11=makeQuery(id+"F4.imprint","IMPRINT",FACE,{"disambiguationData":[TD([[makeQuery(id+"F4.imprint","IMPRINT",EDGE,{"disambiguationData":[TD([[subQ2,-1.0]])],"derivedFrom":subQ1}),1.0]])]});}
            var Q12;
            {var subQ0=sQuery(id+"F4.wireOp",EDGE,"E58");var subQ1=sQuery(id+"F4.wireOp",EDGE,"E43.left");var subQ2=makeQuery(id+"F4.imprint","INTERSECT",VERTEX,{"derivedFrom":[subQ1,subQ0]});Q12=makeQuery(id+"F4.imprint","IMPRINT",FACE,{"disambiguationData":[TD([[makeQuery(id+"F4.imprint","IMPRINT",EDGE,{"disambiguationData":[TD([[subQ2,-1.0]])],"derivedFrom":subQ1}),-1.0]])]});}
            var Q13;
            {var subQ0=sQuery(id+"F4.wireOp",EDGE,"E60.0.1.0");var subQ1=sQuery(id+"F4.wireOp",EDGE,"E47");var subQ2=makeQuery(id+"F4.imprint","INTERSECT",VERTEX,{"derivedFrom":[subQ1,subQ0]});Q13=makeQuery(id+"F4.imprint","IMPRINT",FACE,{"disambiguationData":[TD([[makeQuery(id+"F4.imprint","IMPRINT",EDGE,{"disambiguationData":[TD([[subQ2,-1.0]])],"derivedFrom":subQ1}),1.0]])]});}
            var Q14;
            {var subQ0=sQuery(id+"F4.wireOp",EDGE,"E45");var subQ1=sQuery(id+"F4.wireOp",EDGE,"E43.left");var subQ2=makeQuery(id+"F4.imprint","INTERSECT",VERTEX,{"derivedFrom":[subQ1,subQ0]});Q14=makeQuery(id+"F4.imprint","IMPRINT",FACE,{"disambiguationData":[TD([[makeQuery(id+"F4.imprint","IMPRINT",EDGE,{"disambiguationData":[TD([[subQ2,-1.0]])],"derivedFrom":subQ1}),-1.0]])]});}
            var Q15;
            {var subQ0=sQuery(id+"F4.wireOp",EDGE,"E47");var subQ1=sQuery(id+"F4.wireOp",EDGE,"E45");var subQ2=makeQuery(id+"F4.imprint","INTERSECT",VERTEX,{"derivedFrom":[subQ1,subQ0]});Q15=makeQuery(id+"F4.imprint","IMPRINT",FACE,{"disambiguationData":[TD([[makeQuery(id+"F4.imprint","IMPRINT",EDGE,{"disambiguationData":[TD([[subQ2,1.0]])],"derivedFrom":subQ1}),-1.0]])]});}
            var Q16;
            Q16=sQuery(id+"F0.wireOp",VERTEX,"E5.start");
            extrude(context, id + "F16", {"entities" : qUnion([Q0, Q1, Q2, Q3, Q4, Q5, Q6, Q7, Q8, Q9, Q10, Q11, Q12, Q13, Q14, Q15]), "operationType" : NewBodyOperationType.ADD, "endBound" : BoundingType.UP_TO_VERTEX, "depth" : 25.4 * mm, "endBoundEntityVertex" : qUnion([Q16]), "hasOffset" : true, "offsetDistance" : 12.7 * mm, "offsetOppositeDirection" : true});
        }
        {
            var Q0;
            {var subQ0=sQuery(id+"F4.wireOp",EDGE,"E43.left");Q0=makeQuery(id+"F13.opExtrude","SWEPT_FACE",FACE,{"disambiguationData":[OSD([subQ0]),TDD([makeQuery(id+"F4.imprint","IMPRINT",EDGE,{"disambiguationData":[TD([[makeQuery(id+"F4.imprint","INTERSECT",VERTEX,{"derivedFrom":[sQuery(id+"F4.wireOp",EDGE,"E43.top"),subQ0]}),1.0]])],"derivedFrom":subQ0})])]});}
            var sketch = newSketch(context, id + "F17", { "sketchPlane" : qUnion([Q0])});
            skLineSegment(sketch, "E77", {"start": v(-919.48, 2529.84) * mm, "end": v(-817.88, 2529.84) * mm});
            skFitSpline(sketch, "E78", {"points": [v(-919.48, 2428.24) * mm, v(-898.81, 2471.89) * mm, v(-869.36, 2486.2) * mm, v(-850.85, 2514.8) * mm, v(-817.88, 2529.84) * mm], "startDerivative": vector(52.6, 186.75) * mm, "endDerivative": vector(154.11, 39.47) * mm});
            skSolve(sketch);
        }
        {
            var Q0;
            Q0 = qSketchRegion(id + "F17", true);
            var Q1;
            Q1=makeQuery(id+"F17.imprint","IMPRINT",FACE,{"disambiguationData":[TD([[makeQuery(id+"F17.imprint","IMPRINT",EDGE,{"derivedFrom":sQuery(id+"F17.wireOp",EDGE,"E77")}),-1.0]])]});
            var Q2;
            Q2=sQuery(id+"F4.wireOp",VERTEX,"E43.right.end");
            extrude(context, id + "F18", {"entities" : qUnion([Q0, Q1]), "oppositeDirection" : true, "depth" : 1778 * mm, "endBoundEntityVertex" : qUnion([Q2]), "offsetDistance" : 25.4 * mm});
        }
        {
            var Q0;
            Q0=makeQuery(id+"F17.imprint","IMPRINT",FACE,{"disambiguationData":[TD([[makeQuery(id+"F17.imprint","IMPRINT",EDGE,{"derivedFrom":sQuery(id+"F17.wireOp",EDGE,"E77")}),-1.0]])]});
            extrude(context, id + "F19", {"entities" : qUnion([Q0]), "depth" : 508 * mm, "offsetDistance" : 25.4 * mm});
        }
    });
